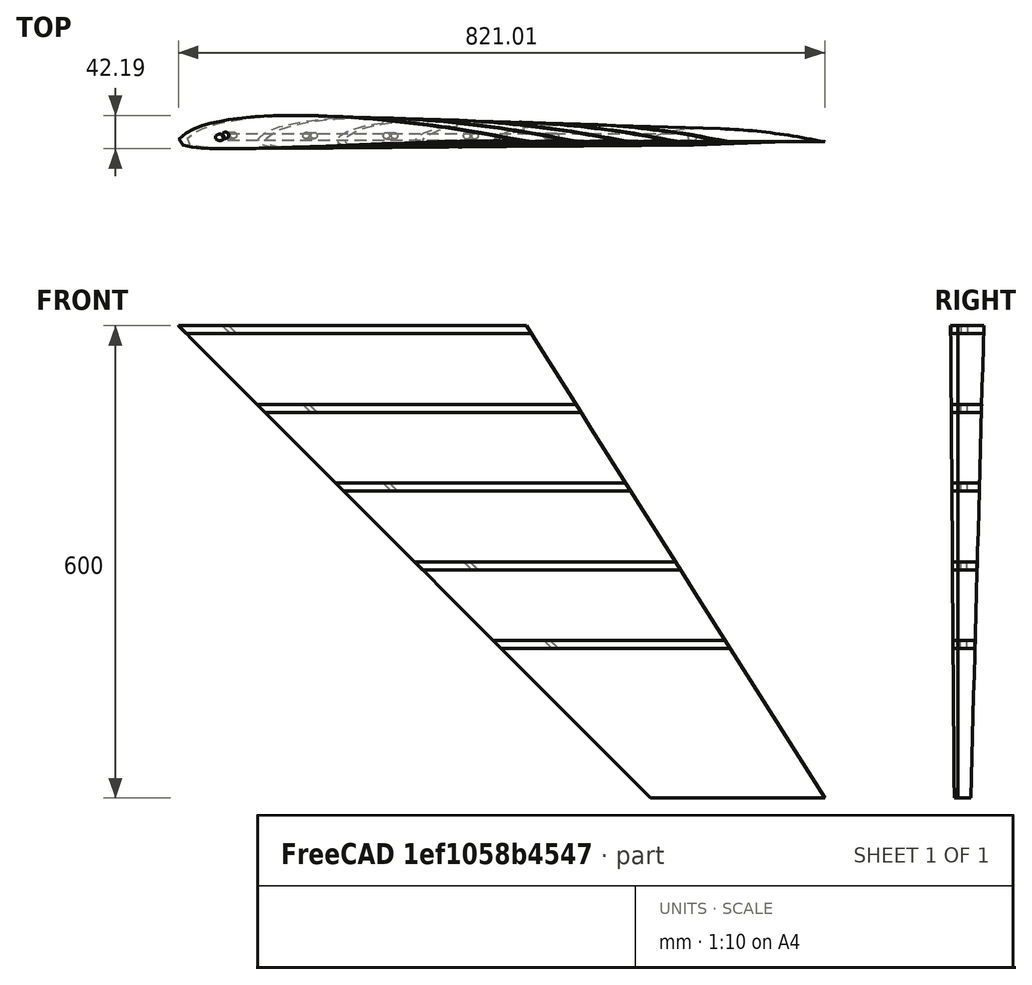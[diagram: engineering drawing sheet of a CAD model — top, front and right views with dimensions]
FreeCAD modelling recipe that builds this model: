
FCSTD DOCUMENT  (FreeCAD 1.0R39109 (Git))
Label: SD7037_the_actual_way
License: All rights reserved
LicenseURL: https://en.wikipedia.org/wiki/All_rights_reserved
objects: Sketcher::SketchObject×38, PartDesign::Pocket×12, PartDesign::AdditiveLoft×7, PartDesign::Body×7, PartDesign::SubtractiveLoft×6, Part::Part2DObjectPython×3, App::DocumentObjectGroup×1, PartDesign::Plane×1
note: 162 computed .brp shape members not serialized (recipe doc carries the construction recipe); baked Part::Feature solids carry a one-line shape summary decoded from their .brp

FEATURE [Part::Part2DObjectPython] Wire  # Draft 2D object (typed FeaturePython)
  Area = 0.0605284
  ChamferSize = 0
  Closed = true
  End = (1,0,0)
  FilletRadius = 0
  Length = 2.02979
  MakeFace = true
  Points = (61) [(1,0,0),(0.99672,0.00042,0),(0.98707,0.0018,0),(0.97146,0.00436,0),(0.95041,0.00811,0),(0.9245,0.01295,0),(0.89425,0.01865,0),(0.86015,0.0249,0),+53 more]
  Start = (1,0,0)
  Subdivisions = 0
FEATURE [App::DocumentObjectGroup] sd7037
  Group = -> [Wire]
FEATURE [Part::Part2DObjectPython] BSpline  label="wingtip"  # Draft 2D object (typed FeaturePython)
  Area = 2965.6
  Closed = true
  MakeFace = true
  Parameterization = 1
  Points = (60) [(221,0,0),(220.275,0.09282,0),(218.142,0.3978,0),(214.693,0.96356,0),(210.041,1.79231,0),(204.315,2.86195,0),(197.629,4.12165,0),(190.093,5.5029,0),+52 more]
FEATURE [Part::Part2DObjectPython] BSpline001  label="wingbase"  # Draft 2D object (typed FeaturePython)
  Area = 11862.4
  Closed = true
  MakeFace = true
  Parameterization = 1
  Points = (60) [(442,0,0),(440.55,0.18564,0),(436.285,0.7956,0),(429.385,1.92712,0),(420.081,3.58462,0),(408.629,5.7239,0),(395.258,8.2433,0),(380.186,11.0058,0),+52 more]
FEATURE [Sketcher::SketchObject] Sketch
  ArcFitTolerance = 1e-06
  FullyConstrained = false
  MakeInternals = false
  Placement = pos=(600,0,-600) rot=(0,0,1;0rad)
  sketch-geometry (123):
    g0: BSplineCurve PolesCount=61 KnotsCount=61 Degree=3 IsPeriodic=1
    g1-g61: Circle [constr] x61 (B-spline internal-alignment scaffolding for g0; pole/knot coordinates omitted)
    g62-g122: GeomPoint [constr] x61 (B-spline internal-alignment scaffolding for g0; pole/knot coordinates omitted)
  constraints (123):
    c: InternalAlignment(g1,g0)
    c: Weight(g1) = 1
    c: InternalAlignment(g2,g0)
    c: Equal(g2,g1)
    c: InternalAlignment(g3,g0)
    c: Equal(g3,g1)
    c: InternalAlignment(g4,g0)
    c: Equal(g4,g1)
    c: InternalAlignment(g5,g0)
    c: Equal(g5,g1)
    c: InternalAlignment(g6,g0)
    c: Equal(g6,g1)
    c: InternalAlignment(g7,g0)
    c: Equal(g7,g1)
    c: InternalAlignment(g8,g0)
    c: Equal(g8,g1)
    c: InternalAlignment(g9,g0)
    c: Equal(g9,g1)
    c: InternalAlignment(g10,g0)
    c: Equal(g10,g1)
    c: InternalAlignment(g11,g0)
    c: Equal(g11,g1)
    c: InternalAlignment(g12,g0)
    c: Equal(g12,g1)
    c: InternalAlignment(g13,g0)
    c: Equal(g13,g1)
    c: InternalAlignment(g14,g0)
    c: Equal(g14,g1)
    c: InternalAlignment(g15,g0)
    c: Equal(g15,g1)
    c: InternalAlignment(g16,g0)
    c: Equal(g16,g1)
    c: InternalAlignment(g17,g0)
    c: Equal(g17,g1)
    c: InternalAlignment(g18,g0)
    c: Equal(g18,g1)
    c: InternalAlignment(g19,g0)
    c: Equal(g19,g1)
    c: InternalAlignment(g20,g0)
    c: Equal(g20,g1)
    c: InternalAlignment(g21,g0)
    c: Equal(g21,g1)
    c: InternalAlignment(g22,g0)
    c: Equal(g22,g1)
    c: InternalAlignment(g23,g0)
    c: Equal(g23,g1)
    c: InternalAlignment(g24,g0)
    c: Equal(g24,g1)
    c: InternalAlignment(g25,g0)
    c: Equal(g25,g1)
    c: InternalAlignment(g26,g0)
    c: Equal(g26,g1)
    c: InternalAlignment(g27,g0)
    c: Equal(g27,g1)
    c: InternalAlignment(g28,g0)
    c: Equal(g28,g1)
    c: InternalAlignment(g29,g0)
    c: Equal(g29,g1)
    c: InternalAlignment(g30,g0)
    c: Equal(g30,g1)
    c: InternalAlignment(g31,g0)
    c: Equal(g31,g1)
    c: InternalAlignment(g32,g0)
    c: Equal(g32,g1)
    c: InternalAlignment(g33,g0)
    c: Equal(g33,g1)
    c: InternalAlignment(g34,g0)
    c: Equal(g34,g1)
    c: InternalAlignment(g35,g0)
    c: Equal(g35,g1)
    c: InternalAlignment(g36,g0)
    c: Equal(g36,g1)
    c: InternalAlignment(g37,g0)
    c: Equal(g37,g1)
    c: InternalAlignment(g38,g0)
    c: Equal(g38,g1)
    c: InternalAlignment(g39,g0)
    c: Equal(g39,g1)
    c: InternalAlignment(g40,g0)
    c: Equal(g40,g1)
    c: InternalAlignment(g41,g0)
    c: Equal(g41,g1)
    c: InternalAlignment(g42,g0)
    c: Equal(g42,g1)
    c: InternalAlignment(g43,g0)
    c: Equal(g43,g1)
    c: InternalAlignment(g44,g0)
    c: Equal(g44,g1)
    c: InternalAlignment(g45,g0)
    c: Equal(g45,g1)
    c: InternalAlignment(g46,g0)
    c: Equal(g46,g1)
    c: InternalAlignment(g47,g0)
    c: Equal(g47,g1)
    c: InternalAlignment(g48,g0)
    c: Equal(g48,g1)
    c: InternalAlignment(g49,g0)
    c: Equal(g49,g1)
    c: InternalAlignment(g50,g0)
    c: Equal(g50,g1)
    c: InternalAlignment(g51,g0)
    c: Equal(g51,g1)
    c: InternalAlignment(g52,g0)
    c: Equal(g52,g1)
    c: InternalAlignment(g53,g0)
    c: Equal(g53,g1)
    c: InternalAlignment(g54,g0)
    c: Equal(g54,g1)
    c: InternalAlignment(g55,g0)
    c: Equal(g55,g1)
    c: InternalAlignment(g56,g0)
    c: Equal(g56,g1)
    c: InternalAlignment(g57,g0)
    c: Equal(g57,g1)
    c: InternalAlignment(g58,g0)
    c: Equal(g58,g1)
    c: InternalAlignment(g59,g0)
    c: Equal(g59,g1)
    c: InternalAlignment(g60,g0)
    c: Equal(g60,g1)
    c: InternalAlignment(g61,g0)
    c: Equal(g61,g1)
    c: InternalAlignment(g62-g122 -> g0) x61
FEATURE [Sketcher::SketchObject] Sketch001
  ArcFitTolerance = 1e-06
  FullyConstrained = false
  MakeInternals = false
  sketch-geometry (123):
    g0: BSplineCurve PolesCount=61 KnotsCount=61 Degree=3 IsPeriodic=1
    g1-g61: Circle [constr] x61 (B-spline internal-alignment scaffolding for g0; pole/knot coordinates omitted)
    g62-g122: GeomPoint [constr] x61 (B-spline internal-alignment scaffolding for g0; pole/knot coordinates omitted)
  constraints (123):
    c: InternalAlignment(g1,g0)
    c: Weight(g1) = 1
    c: InternalAlignment(g2,g0)
    c: Equal(g2,g1)
    c: InternalAlignment(g3,g0)
    c: Equal(g3,g1)
    c: InternalAlignment(g4,g0)
    c: Equal(g4,g1)
    c: InternalAlignment(g5,g0)
    c: Equal(g5,g1)
    c: InternalAlignment(g6,g0)
    c: Equal(g6,g1)
    c: InternalAlignment(g7,g0)
    c: Equal(g7,g1)
    c: InternalAlignment(g8,g0)
    c: Equal(g8,g1)
    c: InternalAlignment(g9,g0)
    c: Equal(g9,g1)
    c: InternalAlignment(g10,g0)
    c: Equal(g10,g1)
    c: InternalAlignment(g11,g0)
    c: Equal(g11,g1)
    c: InternalAlignment(g12,g0)
    c: Equal(g12,g1)
    c: InternalAlignment(g13,g0)
    c: Equal(g13,g1)
    c: InternalAlignment(g14,g0)
    c: Equal(g14,g1)
    c: InternalAlignment(g15,g0)
    c: Equal(g15,g1)
    c: InternalAlignment(g16,g0)
    c: Equal(g16,g1)
    c: InternalAlignment(g17,g0)
    c: Equal(g17,g1)
    c: InternalAlignment(g18,g0)
    c: Equal(g18,g1)
    c: InternalAlignment(g19,g0)
    c: Equal(g19,g1)
    c: InternalAlignment(g20,g0)
    c: Equal(g20,g1)
    c: InternalAlignment(g21,g0)
    c: Equal(g21,g1)
    c: InternalAlignment(g22,g0)
    c: Equal(g22,g1)
    c: InternalAlignment(g23,g0)
    c: Equal(g23,g1)
    c: InternalAlignment(g24,g0)
    c: Equal(g24,g1)
    c: InternalAlignment(g25,g0)
    c: Equal(g25,g1)
    c: InternalAlignment(g26,g0)
    c: Equal(g26,g1)
    c: InternalAlignment(g27,g0)
    c: Equal(g27,g1)
    c: InternalAlignment(g28,g0)
    c: Equal(g28,g1)
    c: InternalAlignment(g29,g0)
    c: Equal(g29,g1)
    c: InternalAlignment(g30,g0)
    c: Equal(g30,g1)
    c: InternalAlignment(g31,g0)
    c: Equal(g31,g1)
    c: InternalAlignment(g32,g0)
    c: Equal(g32,g1)
    c: InternalAlignment(g33,g0)
    c: Equal(g33,g1)
    c: InternalAlignment(g34,g0)
    c: Equal(g34,g1)
    c: InternalAlignment(g35,g0)
    c: Equal(g35,g1)
    c: InternalAlignment(g36,g0)
    c: Equal(g36,g1)
    c: InternalAlignment(g37,g0)
    c: Equal(g37,g1)
    c: InternalAlignment(g38,g0)
    c: Equal(g38,g1)
    c: InternalAlignment(g39,g0)
    c: Equal(g39,g1)
    c: InternalAlignment(g40,g0)
    c: Equal(g40,g1)
    c: InternalAlignment(g41,g0)
    c: Equal(g41,g1)
    c: InternalAlignment(g42,g0)
    c: Equal(g42,g1)
    c: InternalAlignment(g43,g0)
    c: Equal(g43,g1)
    c: InternalAlignment(g44,g0)
    c: Equal(g44,g1)
    c: InternalAlignment(g45,g0)
    c: Equal(g45,g1)
    c: InternalAlignment(g46,g0)
    c: Equal(g46,g1)
    c: InternalAlignment(g47,g0)
    c: Equal(g47,g1)
    c: InternalAlignment(g48,g0)
    c: Equal(g48,g1)
    c: InternalAlignment(g49,g0)
    c: Equal(g49,g1)
    c: InternalAlignment(g50,g0)
    c: Equal(g50,g1)
    c: InternalAlignment(g51,g0)
    c: Equal(g51,g1)
    c: InternalAlignment(g52,g0)
    c: Equal(g52,g1)
    c: InternalAlignment(g53,g0)
    c: Equal(g53,g1)
    c: InternalAlignment(g54,g0)
    c: Equal(g54,g1)
    c: InternalAlignment(g55,g0)
    c: Equal(g55,g1)
    c: InternalAlignment(g56,g0)
    c: Equal(g56,g1)
    c: InternalAlignment(g57,g0)
    c: Equal(g57,g1)
    c: InternalAlignment(g58,g0)
    c: Equal(g58,g1)
    c: InternalAlignment(g59,g0)
    c: Equal(g59,g1)
    c: InternalAlignment(g60,g0)
    c: Equal(g60,g1)
    c: InternalAlignment(g61,g0)
    c: Equal(g61,g1)
    c: InternalAlignment(g62-g122 -> g0) x61
FEATURE [PartDesign::AdditiveLoft] AdditiveLoft
  Closed = false
  Profile = -> Sketch001
  Refine = true
  Ruled = false
  Sections = -> [Sketch]
  Suppressed = false
FEATURE [Sketcher::SketchObject] Sketch002
  ArcFitTolerance = 1e-06
  AttachmentSupport = -> [AdditiveLoft]
  FullyConstrained = true
  MakeInternals = false
  MapMode = 5
  sketch-geometry (1):
    g0: Circle CenterX=60 CenterY=8 CenterZ=0 NormalX=0 NormalY=0 NormalZ=1 AngleXU=0 Radius=4.025
  constraints (3):
    c: Diameter(g0) = 8.05
    c: DistanceX(g-1,g0) = 60
    c: Distance(g0,g-1) = 8
FEATURE [Sketcher::SketchObject] Sketch003
  ArcFitTolerance = 1e-06
  AttachmentSupport = -> [AdditiveLoft]
  FullyConstrained = true
  MakeInternals = false
  MapMode = 5
  Placement = pos=(0,0,-600) rot=(1,0,0;3.14159rad)
  sketch-geometry (1):
    g0: Circle CenterX=673 CenterY=-6.3 CenterZ=0 NormalX=0 NormalY=0 NormalZ=1 AngleXU=0 Radius=4.025
  constraints (3):
    c: Diameter(g0) = 8.05
    c: DistanceX(g-1,g0) = 673
    c: Distance(g0,g-1) = 6.3
FEATURE [PartDesign::SubtractiveLoft] SubtractiveLoft
  BaseFeature = -> AdditiveLoft
  Closed = false
  Profile = -> Sketch002
  Refine = true
  Ruled = false
  Sections = -> [Sketch003]
  Suppressed = false
FEATURE [Sketcher::SketchObject] Sketch004
  ArcFitTolerance = 1e-06
  FullyConstrained = false
  MakeInternals = false
  Placement = pos=(600,0,-600) rot=(0,0,1;0rad)
  sketch-geometry (123):
    g0: BSplineCurve PolesCount=61 KnotsCount=61 Degree=3 IsPeriodic=1
    g1-g61: Circle [constr] x61 (B-spline internal-alignment scaffolding for g0; pole/knot coordinates omitted)
    g62-g122: GeomPoint [constr] x61 (B-spline internal-alignment scaffolding for g0; pole/knot coordinates omitted)
  constraints (123):
    c: InternalAlignment(g1,g0)
    c: Weight(g1) = 1
    c: InternalAlignment(g2,g0)
    c: Equal(g2,g1)
    c: InternalAlignment(g3,g0)
    c: Equal(g3,g1)
    c: InternalAlignment(g4,g0)
    c: Equal(g4,g1)
    c: InternalAlignment(g5,g0)
    c: Equal(g5,g1)
    c: InternalAlignment(g6,g0)
    c: Equal(g6,g1)
    c: InternalAlignment(g7,g0)
    c: Equal(g7,g1)
    c: InternalAlignment(g8,g0)
    c: Equal(g8,g1)
    c: InternalAlignment(g9,g0)
    c: Equal(g9,g1)
    c: InternalAlignment(g10,g0)
    c: Equal(g10,g1)
    c: InternalAlignment(g11,g0)
    c: Equal(g11,g1)
    c: InternalAlignment(g12,g0)
    c: Equal(g12,g1)
    c: InternalAlignment(g13,g0)
    c: Equal(g13,g1)
    c: InternalAlignment(g14,g0)
    c: Equal(g14,g1)
    c: InternalAlignment(g15,g0)
    c: Equal(g15,g1)
    c: InternalAlignment(g16,g0)
    c: Equal(g16,g1)
    c: InternalAlignment(g17,g0)
    c: Equal(g17,g1)
    c: InternalAlignment(g18,g0)
    c: Equal(g18,g1)
    c: InternalAlignment(g19,g0)
    c: Equal(g19,g1)
    c: InternalAlignment(g20,g0)
    c: Equal(g20,g1)
    c: InternalAlignment(g21,g0)
    c: Equal(g21,g1)
    c: InternalAlignment(g22,g0)
    c: Equal(g22,g1)
    c: InternalAlignment(g23,g0)
    c: Equal(g23,g1)
    c: InternalAlignment(g24,g0)
    c: Equal(g24,g1)
    c: InternalAlignment(g25,g0)
    c: Equal(g25,g1)
    c: InternalAlignment(g26,g0)
    c: Equal(g26,g1)
    c: InternalAlignment(g27,g0)
    c: Equal(g27,g1)
    c: InternalAlignment(g28,g0)
    c: Equal(g28,g1)
    c: InternalAlignment(g29,g0)
    c: Equal(g29,g1)
    c: InternalAlignment(g30,g0)
    c: Equal(g30,g1)
    c: InternalAlignment(g31,g0)
    c: Equal(g31,g1)
    c: InternalAlignment(g32,g0)
    c: Equal(g32,g1)
    c: InternalAlignment(g33,g0)
    c: Equal(g33,g1)
    c: InternalAlignment(g34,g0)
    c: Equal(g34,g1)
    c: InternalAlignment(g35,g0)
    c: Equal(g35,g1)
    c: InternalAlignment(g36,g0)
    c: Equal(g36,g1)
    c: InternalAlignment(g37,g0)
    c: Equal(g37,g1)
    c: InternalAlignment(g38,g0)
    c: Equal(g38,g1)
    c: InternalAlignment(g39,g0)
    c: Equal(g39,g1)
    c: InternalAlignment(g40,g0)
    c: Equal(g40,g1)
    c: InternalAlignment(g41,g0)
    c: Equal(g41,g1)
    c: InternalAlignment(g42,g0)
    c: Equal(g42,g1)
    c: InternalAlignment(g43,g0)
    c: Equal(g43,g1)
    c: InternalAlignment(g44,g0)
    c: Equal(g44,g1)
    c: InternalAlignment(g45,g0)
    c: Equal(g45,g1)
    c: InternalAlignment(g46,g0)
    c: Equal(g46,g1)
    c: InternalAlignment(g47,g0)
    c: Equal(g47,g1)
    c: InternalAlignment(g48,g0)
    c: Equal(g48,g1)
    c: InternalAlignment(g49,g0)
    c: Equal(g49,g1)
    c: InternalAlignment(g50,g0)
    c: Equal(g50,g1)
    c: InternalAlignment(g51,g0)
    c: Equal(g51,g1)
    c: InternalAlignment(g52,g0)
    c: Equal(g52,g1)
    c: InternalAlignment(g53,g0)
    c: Equal(g53,g1)
    c: InternalAlignment(g54,g0)
    c: Equal(g54,g1)
    c: InternalAlignment(g55,g0)
    c: Equal(g55,g1)
    c: InternalAlignment(g56,g0)
    c: Equal(g56,g1)
    c: InternalAlignment(g57,g0)
    c: Equal(g57,g1)
    c: InternalAlignment(g58,g0)
    c: Equal(g58,g1)
    c: InternalAlignment(g59,g0)
    c: Equal(g59,g1)
    c: InternalAlignment(g60,g0)
    c: Equal(g60,g1)
    c: InternalAlignment(g61,g0)
    c: Equal(g61,g1)
    c: InternalAlignment(g62-g122 -> g0) x61
FEATURE [Sketcher::SketchObject] Sketch005
  ArcFitTolerance = 1e-06
  FullyConstrained = false
  MakeInternals = false
  sketch-geometry (123):
    g0: BSplineCurve PolesCount=61 KnotsCount=61 Degree=3 IsPeriodic=1
    g1-g61: Circle [constr] x61 (B-spline internal-alignment scaffolding for g0; pole/knot coordinates omitted)
    g62-g122: GeomPoint [constr] x61 (B-spline internal-alignment scaffolding for g0; pole/knot coordinates omitted)
  constraints (123):
    c: InternalAlignment(g1,g0)
    c: Weight(g1) = 1
    c: InternalAlignment(g2,g0)
    c: Equal(g2,g1)
    c: InternalAlignment(g3,g0)
    c: Equal(g3,g1)
    c: InternalAlignment(g4,g0)
    c: Equal(g4,g1)
    c: InternalAlignment(g5,g0)
    c: Equal(g5,g1)
    c: InternalAlignment(g6,g0)
    c: Equal(g6,g1)
    c: InternalAlignment(g7,g0)
    c: Equal(g7,g1)
    c: InternalAlignment(g8,g0)
    c: Equal(g8,g1)
    c: InternalAlignment(g9,g0)
    c: Equal(g9,g1)
    c: InternalAlignment(g10,g0)
    c: Equal(g10,g1)
    c: InternalAlignment(g11,g0)
    c: Equal(g11,g1)
    c: InternalAlignment(g12,g0)
    c: Equal(g12,g1)
    c: InternalAlignment(g13,g0)
    c: Equal(g13,g1)
    c: InternalAlignment(g14,g0)
    c: Equal(g14,g1)
    c: InternalAlignment(g15,g0)
    c: Equal(g15,g1)
    c: InternalAlignment(g16,g0)
    c: Equal(g16,g1)
    c: InternalAlignment(g17,g0)
    c: Equal(g17,g1)
    c: InternalAlignment(g18,g0)
    c: Equal(g18,g1)
    c: InternalAlignment(g19,g0)
    c: Equal(g19,g1)
    c: InternalAlignment(g20,g0)
    c: Equal(g20,g1)
    c: InternalAlignment(g21,g0)
    c: Equal(g21,g1)
    c: InternalAlignment(g22,g0)
    c: Equal(g22,g1)
    c: InternalAlignment(g23,g0)
    c: Equal(g23,g1)
    c: InternalAlignment(g24,g0)
    c: Equal(g24,g1)
    c: InternalAlignment(g25,g0)
    c: Equal(g25,g1)
    c: InternalAlignment(g26,g0)
    c: Equal(g26,g1)
    c: InternalAlignment(g27,g0)
    c: Equal(g27,g1)
    c: InternalAlignment(g28,g0)
    c: Equal(g28,g1)
    c: InternalAlignment(g29,g0)
    c: Equal(g29,g1)
    c: InternalAlignment(g30,g0)
    c: Equal(g30,g1)
    c: InternalAlignment(g31,g0)
    c: Equal(g31,g1)
    c: InternalAlignment(g32,g0)
    c: Equal(g32,g1)
    c: InternalAlignment(g33,g0)
    c: Equal(g33,g1)
    c: InternalAlignment(g34,g0)
    c: Equal(g34,g1)
    c: InternalAlignment(g35,g0)
    c: Equal(g35,g1)
    c: InternalAlignment(g36,g0)
    c: Equal(g36,g1)
    c: InternalAlignment(g37,g0)
    c: Equal(g37,g1)
    c: InternalAlignment(g38,g0)
    c: Equal(g38,g1)
    c: InternalAlignment(g39,g0)
    c: Equal(g39,g1)
    c: InternalAlignment(g40,g0)
    c: Equal(g40,g1)
    c: InternalAlignment(g41,g0)
    c: Equal(g41,g1)
    c: InternalAlignment(g42,g0)
    c: Equal(g42,g1)
    c: InternalAlignment(g43,g0)
    c: Equal(g43,g1)
    c: InternalAlignment(g44,g0)
    c: Equal(g44,g1)
    c: InternalAlignment(g45,g0)
    c: Equal(g45,g1)
    c: InternalAlignment(g46,g0)
    c: Equal(g46,g1)
    c: InternalAlignment(g47,g0)
    c: Equal(g47,g1)
    c: InternalAlignment(g48,g0)
    c: Equal(g48,g1)
    c: InternalAlignment(g49,g0)
    c: Equal(g49,g1)
    c: InternalAlignment(g50,g0)
    c: Equal(g50,g1)
    c: InternalAlignment(g51,g0)
    c: Equal(g51,g1)
    c: InternalAlignment(g52,g0)
    c: Equal(g52,g1)
    c: InternalAlignment(g53,g0)
    c: Equal(g53,g1)
    c: InternalAlignment(g54,g0)
    c: Equal(g54,g1)
    c: InternalAlignment(g55,g0)
    c: Equal(g55,g1)
    c: InternalAlignment(g56,g0)
    c: Equal(g56,g1)
    c: InternalAlignment(g57,g0)
    c: Equal(g57,g1)
    c: InternalAlignment(g58,g0)
    c: Equal(g58,g1)
    c: InternalAlignment(g59,g0)
    c: Equal(g59,g1)
    c: InternalAlignment(g60,g0)
    c: Equal(g60,g1)
    c: InternalAlignment(g61,g0)
    c: Equal(g61,g1)
    c: InternalAlignment(g62-g122 -> g0) x61
FEATURE [PartDesign::AdditiveLoft] AdditiveLoft001
  Closed = false
  Profile = -> Sketch005
  Refine = true
  Ruled = false
  Sections = -> [Sketch004]
  Suppressed = false
FEATURE [Sketcher::SketchObject] Sketch006
  ArcFitTolerance = 1e-06
  AttachmentSupport = -> [AdditiveLoft001]
  FullyConstrained = true
  MakeInternals = false
  MapMode = 5
  sketch-geometry (1):
    g0: Circle CenterX=60 CenterY=8 CenterZ=0 NormalX=0 NormalY=0 NormalZ=1 AngleXU=0 Radius=4.025
  constraints (3):
    c: Diameter(g0) = 8.05
    c: DistanceX(g-1,g0) = 60
    c: Distance(g0,g-1) = 8
FEATURE [Sketcher::SketchObject] Sketch007
  ArcFitTolerance = 1e-06
  AttachmentSupport = -> [AdditiveLoft001]
  FullyConstrained = true
  MakeInternals = false
  MapMode = 5
  Placement = pos=(0,0,-600) rot=(1,0,0;3.14159rad)
  sketch-geometry (1):
    g0: Circle CenterX=673 CenterY=-6.3 CenterZ=0 NormalX=0 NormalY=0 NormalZ=1 AngleXU=0 Radius=4.025
  constraints (3):
    c: Diameter(g0) = 8.05
    c: DistanceX(g-1,g0) = 673
    c: Distance(g0,g-1) = 6.3
FEATURE [PartDesign::SubtractiveLoft] SubtractiveLoft001
  BaseFeature = -> AdditiveLoft001
  Closed = false
  Profile = -> Sketch006
  Refine = true
  Ruled = false
  Sections = -> [Sketch007]
  Suppressed = false
FEATURE [Sketcher::SketchObject] Sketch008
  ArcFitTolerance = 1e-06
  FullyConstrained = false
  MakeInternals = false
  Placement = pos=(600,0,-600) rot=(0,0,1;0rad)
  sketch-geometry (123):
    g0: BSplineCurve PolesCount=61 KnotsCount=61 Degree=3 IsPeriodic=1
    g1-g61: Circle [constr] x61 (B-spline internal-alignment scaffolding for g0; pole/knot coordinates omitted)
    g62-g122: GeomPoint [constr] x61 (B-spline internal-alignment scaffolding for g0; pole/knot coordinates omitted)
  constraints (123):
    c: InternalAlignment(g1,g0)
    c: Weight(g1) = 1
    c: InternalAlignment(g2,g0)
    c: Equal(g2,g1)
    c: InternalAlignment(g3,g0)
    c: Equal(g3,g1)
    c: InternalAlignment(g4,g0)
    c: Equal(g4,g1)
    c: InternalAlignment(g5,g0)
    c: Equal(g5,g1)
    c: InternalAlignment(g6,g0)
    c: Equal(g6,g1)
    c: InternalAlignment(g7,g0)
    c: Equal(g7,g1)
    c: InternalAlignment(g8,g0)
    c: Equal(g8,g1)
    c: InternalAlignment(g9,g0)
    c: Equal(g9,g1)
    c: InternalAlignment(g10,g0)
    c: Equal(g10,g1)
    c: InternalAlignment(g11,g0)
    c: Equal(g11,g1)
    c: InternalAlignment(g12,g0)
    c: Equal(g12,g1)
    c: InternalAlignment(g13,g0)
    c: Equal(g13,g1)
    c: InternalAlignment(g14,g0)
    c: Equal(g14,g1)
    c: InternalAlignment(g15,g0)
    c: Equal(g15,g1)
    c: InternalAlignment(g16,g0)
    c: Equal(g16,g1)
    c: InternalAlignment(g17,g0)
    c: Equal(g17,g1)
    c: InternalAlignment(g18,g0)
    c: Equal(g18,g1)
    c: InternalAlignment(g19,g0)
    c: Equal(g19,g1)
    c: InternalAlignment(g20,g0)
    c: Equal(g20,g1)
    c: InternalAlignment(g21,g0)
    c: Equal(g21,g1)
    c: InternalAlignment(g22,g0)
    c: Equal(g22,g1)
    c: InternalAlignment(g23,g0)
    c: Equal(g23,g1)
    c: InternalAlignment(g24,g0)
    c: Equal(g24,g1)
    c: InternalAlignment(g25,g0)
    c: Equal(g25,g1)
    c: InternalAlignment(g26,g0)
    c: Equal(g26,g1)
    c: InternalAlignment(g27,g0)
    c: Equal(g27,g1)
    c: InternalAlignment(g28,g0)
    c: Equal(g28,g1)
    c: InternalAlignment(g29,g0)
    c: Equal(g29,g1)
    c: InternalAlignment(g30,g0)
    c: Equal(g30,g1)
    c: InternalAlignment(g31,g0)
    c: Equal(g31,g1)
    c: InternalAlignment(g32,g0)
    c: Equal(g32,g1)
    c: InternalAlignment(g33,g0)
    c: Equal(g33,g1)
    c: InternalAlignment(g34,g0)
    c: Equal(g34,g1)
    c: InternalAlignment(g35,g0)
    c: Equal(g35,g1)
    c: InternalAlignment(g36,g0)
    c: Equal(g36,g1)
    c: InternalAlignment(g37,g0)
    c: Equal(g37,g1)
    c: InternalAlignment(g38,g0)
    c: Equal(g38,g1)
    c: InternalAlignment(g39,g0)
    c: Equal(g39,g1)
    c: InternalAlignment(g40,g0)
    c: Equal(g40,g1)
    c: InternalAlignment(g41,g0)
    c: Equal(g41,g1)
    c: InternalAlignment(g42,g0)
    c: Equal(g42,g1)
    c: InternalAlignment(g43,g0)
    c: Equal(g43,g1)
    c: InternalAlignment(g44,g0)
    c: Equal(g44,g1)
    c: InternalAlignment(g45,g0)
    c: Equal(g45,g1)
    c: InternalAlignment(g46,g0)
    c: Equal(g46,g1)
    c: InternalAlignment(g47,g0)
    c: Equal(g47,g1)
    c: InternalAlignment(g48,g0)
    c: Equal(g48,g1)
    c: InternalAlignment(g49,g0)
    c: Equal(g49,g1)
    c: InternalAlignment(g50,g0)
    c: Equal(g50,g1)
    c: InternalAlignment(g51,g0)
    c: Equal(g51,g1)
    c: InternalAlignment(g52,g0)
    c: Equal(g52,g1)
    c: InternalAlignment(g53,g0)
    c: Equal(g53,g1)
    c: InternalAlignment(g54,g0)
    c: Equal(g54,g1)
    c: InternalAlignment(g55,g0)
    c: Equal(g55,g1)
    c: InternalAlignment(g56,g0)
    c: Equal(g56,g1)
    c: InternalAlignment(g57,g0)
    c: Equal(g57,g1)
    c: InternalAlignment(g58,g0)
    c: Equal(g58,g1)
    c: InternalAlignment(g59,g0)
    c: Equal(g59,g1)
    c: InternalAlignment(g60,g0)
    c: Equal(g60,g1)
    c: InternalAlignment(g61,g0)
    c: Equal(g61,g1)
    c: InternalAlignment(g62-g122 -> g0) x61
FEATURE [Sketcher::SketchObject] Sketch009
  ArcFitTolerance = 1e-06
  FullyConstrained = false
  MakeInternals = false
  sketch-geometry (123):
    g0: BSplineCurve PolesCount=61 KnotsCount=61 Degree=3 IsPeriodic=1
    g1-g61: Circle [constr] x61 (B-spline internal-alignment scaffolding for g0; pole/knot coordinates omitted)
    g62-g122: GeomPoint [constr] x61 (B-spline internal-alignment scaffolding for g0; pole/knot coordinates omitted)
  constraints (123):
    c: InternalAlignment(g1,g0)
    c: Weight(g1) = 1
    c: InternalAlignment(g2,g0)
    c: Equal(g2,g1)
    c: InternalAlignment(g3,g0)
    c: Equal(g3,g1)
    c: InternalAlignment(g4,g0)
    c: Equal(g4,g1)
    c: InternalAlignment(g5,g0)
    c: Equal(g5,g1)
    c: InternalAlignment(g6,g0)
    c: Equal(g6,g1)
    c: InternalAlignment(g7,g0)
    c: Equal(g7,g1)
    c: InternalAlignment(g8,g0)
    c: Equal(g8,g1)
    c: InternalAlignment(g9,g0)
    c: Equal(g9,g1)
    c: InternalAlignment(g10,g0)
    c: Equal(g10,g1)
    c: InternalAlignment(g11,g0)
    c: Equal(g11,g1)
    c: InternalAlignment(g12,g0)
    c: Equal(g12,g1)
    c: InternalAlignment(g13,g0)
    c: Equal(g13,g1)
    c: InternalAlignment(g14,g0)
    c: Equal(g14,g1)
    c: InternalAlignment(g15,g0)
    c: Equal(g15,g1)
    c: InternalAlignment(g16,g0)
    c: Equal(g16,g1)
    c: InternalAlignment(g17,g0)
    c: Equal(g17,g1)
    c: InternalAlignment(g18,g0)
    c: Equal(g18,g1)
    c: InternalAlignment(g19,g0)
    c: Equal(g19,g1)
    c: InternalAlignment(g20,g0)
    c: Equal(g20,g1)
    c: InternalAlignment(g21,g0)
    c: Equal(g21,g1)
    c: InternalAlignment(g22,g0)
    c: Equal(g22,g1)
    c: InternalAlignment(g23,g0)
    c: Equal(g23,g1)
    c: InternalAlignment(g24,g0)
    c: Equal(g24,g1)
    c: InternalAlignment(g25,g0)
    c: Equal(g25,g1)
    c: InternalAlignment(g26,g0)
    c: Equal(g26,g1)
    c: InternalAlignment(g27,g0)
    c: Equal(g27,g1)
    c: InternalAlignment(g28,g0)
    c: Equal(g28,g1)
    c: InternalAlignment(g29,g0)
    c: Equal(g29,g1)
    c: InternalAlignment(g30,g0)
    c: Equal(g30,g1)
    c: InternalAlignment(g31,g0)
    c: Equal(g31,g1)
    c: InternalAlignment(g32,g0)
    c: Equal(g32,g1)
    c: InternalAlignment(g33,g0)
    c: Equal(g33,g1)
    c: InternalAlignment(g34,g0)
    c: Equal(g34,g1)
    c: InternalAlignment(g35,g0)
    c: Equal(g35,g1)
    c: InternalAlignment(g36,g0)
    c: Equal(g36,g1)
    c: InternalAlignment(g37,g0)
    c: Equal(g37,g1)
    c: InternalAlignment(g38,g0)
    c: Equal(g38,g1)
    c: InternalAlignment(g39,g0)
    c: Equal(g39,g1)
    c: InternalAlignment(g40,g0)
    c: Equal(g40,g1)
    c: InternalAlignment(g41,g0)
    c: Equal(g41,g1)
    c: InternalAlignment(g42,g0)
    c: Equal(g42,g1)
    c: InternalAlignment(g43,g0)
    c: Equal(g43,g1)
    c: InternalAlignment(g44,g0)
    c: Equal(g44,g1)
    c: InternalAlignment(g45,g0)
    c: Equal(g45,g1)
    c: InternalAlignment(g46,g0)
    c: Equal(g46,g1)
    c: InternalAlignment(g47,g0)
    c: Equal(g47,g1)
    c: InternalAlignment(g48,g0)
    c: Equal(g48,g1)
    c: InternalAlignment(g49,g0)
    c: Equal(g49,g1)
    c: InternalAlignment(g50,g0)
    c: Equal(g50,g1)
    c: InternalAlignment(g51,g0)
    c: Equal(g51,g1)
    c: InternalAlignment(g52,g0)
    c: Equal(g52,g1)
    c: InternalAlignment(g53,g0)
    c: Equal(g53,g1)
    c: InternalAlignment(g54,g0)
    c: Equal(g54,g1)
    c: InternalAlignment(g55,g0)
    c: Equal(g55,g1)
    c: InternalAlignment(g56,g0)
    c: Equal(g56,g1)
    c: InternalAlignment(g57,g0)
    c: Equal(g57,g1)
    c: InternalAlignment(g58,g0)
    c: Equal(g58,g1)
    c: InternalAlignment(g59,g0)
    c: Equal(g59,g1)
    c: InternalAlignment(g60,g0)
    c: Equal(g60,g1)
    c: InternalAlignment(g61,g0)
    c: Equal(g61,g1)
    c: InternalAlignment(g62-g122 -> g0) x61
FEATURE [PartDesign::AdditiveLoft] AdditiveLoft002
  Closed = false
  Profile = -> Sketch009
  Refine = true
  Ruled = false
  Sections = -> [Sketch008]
  Suppressed = false
FEATURE [Sketcher::SketchObject] Sketch010
  ArcFitTolerance = 1e-06
  AttachmentSupport = -> [AdditiveLoft002]
  FullyConstrained = true
  MakeInternals = false
  MapMode = 5
  sketch-geometry (1):
    g0: Circle CenterX=60 CenterY=8 CenterZ=0 NormalX=0 NormalY=0 NormalZ=1 AngleXU=0 Radius=4.025
  constraints (3):
    c: Diameter(g0) = 8.05
    c: DistanceX(g-1,g0) = 60
    c: Distance(g0,g-1) = 8
FEATURE [Sketcher::SketchObject] Sketch011
  ArcFitTolerance = 1e-06
  AttachmentSupport = -> [AdditiveLoft002]
  FullyConstrained = true
  MakeInternals = false
  MapMode = 5
  Placement = pos=(0,0,-600) rot=(1,0,0;3.14159rad)
  sketch-geometry (1):
    g0: Circle CenterX=673 CenterY=-6.3 CenterZ=0 NormalX=0 NormalY=0 NormalZ=1 AngleXU=0 Radius=4.025
  constraints (3):
    c: Diameter(g0) = 8.05
    c: DistanceX(g-1,g0) = 673
    c: Distance(g0,g-1) = 6.3
FEATURE [PartDesign::SubtractiveLoft] SubtractiveLoft002
  BaseFeature = -> AdditiveLoft002
  Closed = false
  Profile = -> Sketch010
  Refine = true
  Ruled = false
  Sections = -> [Sketch011]
  Suppressed = false
FEATURE [Sketcher::SketchObject] Sketch012
  ArcFitTolerance = 1e-06
  FullyConstrained = false
  MakeInternals = false
  Placement = pos=(600,0,-600) rot=(0,0,1;0rad)
  sketch-geometry (123):
    g0: BSplineCurve PolesCount=61 KnotsCount=61 Degree=3 IsPeriodic=1
    g1-g61: Circle [constr] x61 (B-spline internal-alignment scaffolding for g0; pole/knot coordinates omitted)
    g62-g122: GeomPoint [constr] x61 (B-spline internal-alignment scaffolding for g0; pole/knot coordinates omitted)
  constraints (123):
    c: InternalAlignment(g1,g0)
    c: Weight(g1) = 1
    c: InternalAlignment(g2,g0)
    c: Equal(g2,g1)
    c: InternalAlignment(g3,g0)
    c: Equal(g3,g1)
    c: InternalAlignment(g4,g0)
    c: Equal(g4,g1)
    c: InternalAlignment(g5,g0)
    c: Equal(g5,g1)
    c: InternalAlignment(g6,g0)
    c: Equal(g6,g1)
    c: InternalAlignment(g7,g0)
    c: Equal(g7,g1)
    c: InternalAlignment(g8,g0)
    c: Equal(g8,g1)
    c: InternalAlignment(g9,g0)
    c: Equal(g9,g1)
    c: InternalAlignment(g10,g0)
    c: Equal(g10,g1)
    c: InternalAlignment(g11,g0)
    c: Equal(g11,g1)
    c: InternalAlignment(g12,g0)
    c: Equal(g12,g1)
    c: InternalAlignment(g13,g0)
    c: Equal(g13,g1)
    c: InternalAlignment(g14,g0)
    c: Equal(g14,g1)
    c: InternalAlignment(g15,g0)
    c: Equal(g15,g1)
    c: InternalAlignment(g16,g0)
    c: Equal(g16,g1)
    c: InternalAlignment(g17,g0)
    c: Equal(g17,g1)
    c: InternalAlignment(g18,g0)
    c: Equal(g18,g1)
    c: InternalAlignment(g19,g0)
    c: Equal(g19,g1)
    c: InternalAlignment(g20,g0)
    c: Equal(g20,g1)
    c: InternalAlignment(g21,g0)
    c: Equal(g21,g1)
    c: InternalAlignment(g22,g0)
    c: Equal(g22,g1)
    c: InternalAlignment(g23,g0)
    c: Equal(g23,g1)
    c: InternalAlignment(g24,g0)
    c: Equal(g24,g1)
    c: InternalAlignment(g25,g0)
    c: Equal(g25,g1)
    c: InternalAlignment(g26,g0)
    c: Equal(g26,g1)
    c: InternalAlignment(g27,g0)
    c: Equal(g27,g1)
    c: InternalAlignment(g28,g0)
    c: Equal(g28,g1)
    c: InternalAlignment(g29,g0)
    c: Equal(g29,g1)
    c: InternalAlignment(g30,g0)
    c: Equal(g30,g1)
    c: InternalAlignment(g31,g0)
    c: Equal(g31,g1)
    c: InternalAlignment(g32,g0)
    c: Equal(g32,g1)
    c: InternalAlignment(g33,g0)
    c: Equal(g33,g1)
    c: InternalAlignment(g34,g0)
    c: Equal(g34,g1)
    c: InternalAlignment(g35,g0)
    c: Equal(g35,g1)
    c: InternalAlignment(g36,g0)
    c: Equal(g36,g1)
    c: InternalAlignment(g37,g0)
    c: Equal(g37,g1)
    c: InternalAlignment(g38,g0)
    c: Equal(g38,g1)
    c: InternalAlignment(g39,g0)
    c: Equal(g39,g1)
    c: InternalAlignment(g40,g0)
    c: Equal(g40,g1)
    c: InternalAlignment(g41,g0)
    c: Equal(g41,g1)
    c: InternalAlignment(g42,g0)
    c: Equal(g42,g1)
    c: InternalAlignment(g43,g0)
    c: Equal(g43,g1)
    c: InternalAlignment(g44,g0)
    c: Equal(g44,g1)
    c: InternalAlignment(g45,g0)
    c: Equal(g45,g1)
    c: InternalAlignment(g46,g0)
    c: Equal(g46,g1)
    c: InternalAlignment(g47,g0)
    c: Equal(g47,g1)
    c: InternalAlignment(g48,g0)
    c: Equal(g48,g1)
    c: InternalAlignment(g49,g0)
    c: Equal(g49,g1)
    c: InternalAlignment(g50,g0)
    c: Equal(g50,g1)
    c: InternalAlignment(g51,g0)
    c: Equal(g51,g1)
    c: InternalAlignment(g52,g0)
    c: Equal(g52,g1)
    c: InternalAlignment(g53,g0)
    c: Equal(g53,g1)
    c: InternalAlignment(g54,g0)
    c: Equal(g54,g1)
    c: InternalAlignment(g55,g0)
    c: Equal(g55,g1)
    c: InternalAlignment(g56,g0)
    c: Equal(g56,g1)
    c: InternalAlignment(g57,g0)
    c: Equal(g57,g1)
    c: InternalAlignment(g58,g0)
    c: Equal(g58,g1)
    c: InternalAlignment(g59,g0)
    c: Equal(g59,g1)
    c: InternalAlignment(g60,g0)
    c: Equal(g60,g1)
    c: InternalAlignment(g61,g0)
    c: Equal(g61,g1)
    c: InternalAlignment(g62-g122 -> g0) x61
FEATURE [Sketcher::SketchObject] Sketch013
  ArcFitTolerance = 1e-06
  FullyConstrained = false
  MakeInternals = false
  sketch-geometry (123):
    g0: BSplineCurve PolesCount=61 KnotsCount=61 Degree=3 IsPeriodic=1
    g1-g61: Circle [constr] x61 (B-spline internal-alignment scaffolding for g0; pole/knot coordinates omitted)
    g62-g122: GeomPoint [constr] x61 (B-spline internal-alignment scaffolding for g0; pole/knot coordinates omitted)
  constraints (123):
    c: InternalAlignment(g1,g0)
    c: Weight(g1) = 1
    c: InternalAlignment(g2,g0)
    c: Equal(g2,g1)
    c: InternalAlignment(g3,g0)
    c: Equal(g3,g1)
    c: InternalAlignment(g4,g0)
    c: Equal(g4,g1)
    c: InternalAlignment(g5,g0)
    c: Equal(g5,g1)
    c: InternalAlignment(g6,g0)
    c: Equal(g6,g1)
    c: InternalAlignment(g7,g0)
    c: Equal(g7,g1)
    c: InternalAlignment(g8,g0)
    c: Equal(g8,g1)
    c: InternalAlignment(g9,g0)
    c: Equal(g9,g1)
    c: InternalAlignment(g10,g0)
    c: Equal(g10,g1)
    c: InternalAlignment(g11,g0)
    c: Equal(g11,g1)
    c: InternalAlignment(g12,g0)
    c: Equal(g12,g1)
    c: InternalAlignment(g13,g0)
    c: Equal(g13,g1)
    c: InternalAlignment(g14,g0)
    c: Equal(g14,g1)
    c: InternalAlignment(g15,g0)
    c: Equal(g15,g1)
    c: InternalAlignment(g16,g0)
    c: Equal(g16,g1)
    c: InternalAlignment(g17,g0)
    c: Equal(g17,g1)
    c: InternalAlignment(g18,g0)
    c: Equal(g18,g1)
    c: InternalAlignment(g19,g0)
    c: Equal(g19,g1)
    c: InternalAlignment(g20,g0)
    c: Equal(g20,g1)
    c: InternalAlignment(g21,g0)
    c: Equal(g21,g1)
    c: InternalAlignment(g22,g0)
    c: Equal(g22,g1)
    c: InternalAlignment(g23,g0)
    c: Equal(g23,g1)
    c: InternalAlignment(g24,g0)
    c: Equal(g24,g1)
    c: InternalAlignment(g25,g0)
    c: Equal(g25,g1)
    c: InternalAlignment(g26,g0)
    c: Equal(g26,g1)
    c: InternalAlignment(g27,g0)
    c: Equal(g27,g1)
    c: InternalAlignment(g28,g0)
    c: Equal(g28,g1)
    c: InternalAlignment(g29,g0)
    c: Equal(g29,g1)
    c: InternalAlignment(g30,g0)
    c: Equal(g30,g1)
    c: InternalAlignment(g31,g0)
    c: Equal(g31,g1)
    c: InternalAlignment(g32,g0)
    c: Equal(g32,g1)
    c: InternalAlignment(g33,g0)
    c: Equal(g33,g1)
    c: InternalAlignment(g34,g0)
    c: Equal(g34,g1)
    c: InternalAlignment(g35,g0)
    c: Equal(g35,g1)
    c: InternalAlignment(g36,g0)
    c: Equal(g36,g1)
    c: InternalAlignment(g37,g0)
    c: Equal(g37,g1)
    c: InternalAlignment(g38,g0)
    c: Equal(g38,g1)
    c: InternalAlignment(g39,g0)
    c: Equal(g39,g1)
    c: InternalAlignment(g40,g0)
    c: Equal(g40,g1)
    c: InternalAlignment(g41,g0)
    c: Equal(g41,g1)
    c: InternalAlignment(g42,g0)
    c: Equal(g42,g1)
    c: InternalAlignment(g43,g0)
    c: Equal(g43,g1)
    c: InternalAlignment(g44,g0)
    c: Equal(g44,g1)
    c: InternalAlignment(g45,g0)
    c: Equal(g45,g1)
    c: InternalAlignment(g46,g0)
    c: Equal(g46,g1)
    c: InternalAlignment(g47,g0)
    c: Equal(g47,g1)
    c: InternalAlignment(g48,g0)
    c: Equal(g48,g1)
    c: InternalAlignment(g49,g0)
    c: Equal(g49,g1)
    c: InternalAlignment(g50,g0)
    c: Equal(g50,g1)
    c: InternalAlignment(g51,g0)
    c: Equal(g51,g1)
    c: InternalAlignment(g52,g0)
    c: Equal(g52,g1)
    c: InternalAlignment(g53,g0)
    c: Equal(g53,g1)
    c: InternalAlignment(g54,g0)
    c: Equal(g54,g1)
    c: InternalAlignment(g55,g0)
    c: Equal(g55,g1)
    c: InternalAlignment(g56,g0)
    c: Equal(g56,g1)
    c: InternalAlignment(g57,g0)
    c: Equal(g57,g1)
    c: InternalAlignment(g58,g0)
    c: Equal(g58,g1)
    c: InternalAlignment(g59,g0)
    c: Equal(g59,g1)
    c: InternalAlignment(g60,g0)
    c: Equal(g60,g1)
    c: InternalAlignment(g61,g0)
    c: Equal(g61,g1)
    c: InternalAlignment(g62-g122 -> g0) x61
FEATURE [PartDesign::AdditiveLoft] AdditiveLoft003
  Closed = false
  Profile = -> Sketch013
  Refine = true
  Ruled = false
  Sections = -> [Sketch012]
  Suppressed = false
FEATURE [Sketcher::SketchObject] Sketch014
  ArcFitTolerance = 1e-06
  AttachmentSupport = -> [AdditiveLoft003]
  FullyConstrained = true
  MakeInternals = false
  MapMode = 5
  sketch-geometry (1):
    g0: Circle CenterX=60 CenterY=8 CenterZ=0 NormalX=0 NormalY=0 NormalZ=1 AngleXU=0 Radius=4.025
  constraints (3):
    c: Diameter(g0) = 8.05
    c: DistanceX(g-1,g0) = 60
    c: Distance(g0,g-1) = 8
FEATURE [Sketcher::SketchObject] Sketch015
  ArcFitTolerance = 1e-06
  AttachmentSupport = -> [AdditiveLoft003]
  FullyConstrained = true
  MakeInternals = false
  MapMode = 5
  Placement = pos=(0,0,-600) rot=(1,0,0;3.14159rad)
  sketch-geometry (1):
    g0: Circle CenterX=673 CenterY=-6.3 CenterZ=0 NormalX=0 NormalY=0 NormalZ=1 AngleXU=0 Radius=4.025
  constraints (3):
    c: Diameter(g0) = 8.05
    c: DistanceX(g-1,g0) = 673
    c: Distance(g0,g-1) = 6.3
FEATURE [PartDesign::SubtractiveLoft] SubtractiveLoft003
  BaseFeature = -> AdditiveLoft003
  Closed = false
  Profile = -> Sketch014
  Refine = true
  Ruled = false
  Sections = -> [Sketch015]
  Suppressed = false
FEATURE [Sketcher::SketchObject] Sketch016
  ArcFitTolerance = 1e-06
  FullyConstrained = false
  MakeInternals = false
  Placement = pos=(600,0,-600) rot=(0,0,1;0rad)
  sketch-geometry (123):
    g0: BSplineCurve PolesCount=61 KnotsCount=61 Degree=3 IsPeriodic=1
    g1-g61: Circle [constr] x61 (B-spline internal-alignment scaffolding for g0; pole/knot coordinates omitted)
    g62-g122: GeomPoint [constr] x61 (B-spline internal-alignment scaffolding for g0; pole/knot coordinates omitted)
  constraints (123):
    c: InternalAlignment(g1,g0)
    c: Weight(g1) = 1
    c: InternalAlignment(g2,g0)
    c: Equal(g2,g1)
    c: InternalAlignment(g3,g0)
    c: Equal(g3,g1)
    c: InternalAlignment(g4,g0)
    c: Equal(g4,g1)
    c: InternalAlignment(g5,g0)
    c: Equal(g5,g1)
    c: InternalAlignment(g6,g0)
    c: Equal(g6,g1)
    c: InternalAlignment(g7,g0)
    c: Equal(g7,g1)
    c: InternalAlignment(g8,g0)
    c: Equal(g8,g1)
    c: InternalAlignment(g9,g0)
    c: Equal(g9,g1)
    c: InternalAlignment(g10,g0)
    c: Equal(g10,g1)
    c: InternalAlignment(g11,g0)
    c: Equal(g11,g1)
    c: InternalAlignment(g12,g0)
    c: Equal(g12,g1)
    c: InternalAlignment(g13,g0)
    c: Equal(g13,g1)
    c: InternalAlignment(g14,g0)
    c: Equal(g14,g1)
    c: InternalAlignment(g15,g0)
    c: Equal(g15,g1)
    c: InternalAlignment(g16,g0)
    c: Equal(g16,g1)
    c: InternalAlignment(g17,g0)
    c: Equal(g17,g1)
    c: InternalAlignment(g18,g0)
    c: Equal(g18,g1)
    c: InternalAlignment(g19,g0)
    c: Equal(g19,g1)
    c: InternalAlignment(g20,g0)
    c: Equal(g20,g1)
    c: InternalAlignment(g21,g0)
    c: Equal(g21,g1)
    c: InternalAlignment(g22,g0)
    c: Equal(g22,g1)
    c: InternalAlignment(g23,g0)
    c: Equal(g23,g1)
    c: InternalAlignment(g24,g0)
    c: Equal(g24,g1)
    c: InternalAlignment(g25,g0)
    c: Equal(g25,g1)
    c: InternalAlignment(g26,g0)
    c: Equal(g26,g1)
    c: InternalAlignment(g27,g0)
    c: Equal(g27,g1)
    c: InternalAlignment(g28,g0)
    c: Equal(g28,g1)
    c: InternalAlignment(g29,g0)
    c: Equal(g29,g1)
    c: InternalAlignment(g30,g0)
    c: Equal(g30,g1)
    c: InternalAlignment(g31,g0)
    c: Equal(g31,g1)
    c: InternalAlignment(g32,g0)
    c: Equal(g32,g1)
    c: InternalAlignment(g33,g0)
    c: Equal(g33,g1)
    c: InternalAlignment(g34,g0)
    c: Equal(g34,g1)
    c: InternalAlignment(g35,g0)
    c: Equal(g35,g1)
    c: InternalAlignment(g36,g0)
    c: Equal(g36,g1)
    c: InternalAlignment(g37,g0)
    c: Equal(g37,g1)
    c: InternalAlignment(g38,g0)
    c: Equal(g38,g1)
    c: InternalAlignment(g39,g0)
    c: Equal(g39,g1)
    c: InternalAlignment(g40,g0)
    c: Equal(g40,g1)
    c: InternalAlignment(g41,g0)
    c: Equal(g41,g1)
    c: InternalAlignment(g42,g0)
    c: Equal(g42,g1)
    c: InternalAlignment(g43,g0)
    c: Equal(g43,g1)
    c: InternalAlignment(g44,g0)
    c: Equal(g44,g1)
    c: InternalAlignment(g45,g0)
    c: Equal(g45,g1)
    c: InternalAlignment(g46,g0)
    c: Equal(g46,g1)
    c: InternalAlignment(g47,g0)
    c: Equal(g47,g1)
    c: InternalAlignment(g48,g0)
    c: Equal(g48,g1)
    c: InternalAlignment(g49,g0)
    c: Equal(g49,g1)
    c: InternalAlignment(g50,g0)
    c: Equal(g50,g1)
    c: InternalAlignment(g51,g0)
    c: Equal(g51,g1)
    c: InternalAlignment(g52,g0)
    c: Equal(g52,g1)
    c: InternalAlignment(g53,g0)
    c: Equal(g53,g1)
    c: InternalAlignment(g54,g0)
    c: Equal(g54,g1)
    c: InternalAlignment(g55,g0)
    c: Equal(g55,g1)
    c: InternalAlignment(g56,g0)
    c: Equal(g56,g1)
    c: InternalAlignment(g57,g0)
    c: Equal(g57,g1)
    c: InternalAlignment(g58,g0)
    c: Equal(g58,g1)
    c: InternalAlignment(g59,g0)
    c: Equal(g59,g1)
    c: InternalAlignment(g60,g0)
    c: Equal(g60,g1)
    c: InternalAlignment(g61,g0)
    c: Equal(g61,g1)
    c: InternalAlignment(g62-g122 -> g0) x61
FEATURE [Sketcher::SketchObject] Sketch017
  ArcFitTolerance = 1e-06
  FullyConstrained = false
  MakeInternals = false
  sketch-geometry (123):
    g0: BSplineCurve PolesCount=61 KnotsCount=61 Degree=3 IsPeriodic=1
    g1-g61: Circle [constr] x61 (B-spline internal-alignment scaffolding for g0; pole/knot coordinates omitted)
    g62-g122: GeomPoint [constr] x61 (B-spline internal-alignment scaffolding for g0; pole/knot coordinates omitted)
  constraints (123):
    c: InternalAlignment(g1,g0)
    c: Weight(g1) = 1
    c: InternalAlignment(g2,g0)
    c: Equal(g2,g1)
    c: InternalAlignment(g3,g0)
    c: Equal(g3,g1)
    c: InternalAlignment(g4,g0)
    c: Equal(g4,g1)
    c: InternalAlignment(g5,g0)
    c: Equal(g5,g1)
    c: InternalAlignment(g6,g0)
    c: Equal(g6,g1)
    c: InternalAlignment(g7,g0)
    c: Equal(g7,g1)
    c: InternalAlignment(g8,g0)
    c: Equal(g8,g1)
    c: InternalAlignment(g9,g0)
    c: Equal(g9,g1)
    c: InternalAlignment(g10,g0)
    c: Equal(g10,g1)
    c: InternalAlignment(g11,g0)
    c: Equal(g11,g1)
    c: InternalAlignment(g12,g0)
    c: Equal(g12,g1)
    c: InternalAlignment(g13,g0)
    c: Equal(g13,g1)
    c: InternalAlignment(g14,g0)
    c: Equal(g14,g1)
    c: InternalAlignment(g15,g0)
    c: Equal(g15,g1)
    c: InternalAlignment(g16,g0)
    c: Equal(g16,g1)
    c: InternalAlignment(g17,g0)
    c: Equal(g17,g1)
    c: InternalAlignment(g18,g0)
    c: Equal(g18,g1)
    c: InternalAlignment(g19,g0)
    c: Equal(g19,g1)
    c: InternalAlignment(g20,g0)
    c: Equal(g20,g1)
    c: InternalAlignment(g21,g0)
    c: Equal(g21,g1)
    c: InternalAlignment(g22,g0)
    c: Equal(g22,g1)
    c: InternalAlignment(g23,g0)
    c: Equal(g23,g1)
    c: InternalAlignment(g24,g0)
    c: Equal(g24,g1)
    c: InternalAlignment(g25,g0)
    c: Equal(g25,g1)
    c: InternalAlignment(g26,g0)
    c: Equal(g26,g1)
    c: InternalAlignment(g27,g0)
    c: Equal(g27,g1)
    c: InternalAlignment(g28,g0)
    c: Equal(g28,g1)
    c: InternalAlignment(g29,g0)
    c: Equal(g29,g1)
    c: InternalAlignment(g30,g0)
    c: Equal(g30,g1)
    c: InternalAlignment(g31,g0)
    c: Equal(g31,g1)
    c: InternalAlignment(g32,g0)
    c: Equal(g32,g1)
    c: InternalAlignment(g33,g0)
    c: Equal(g33,g1)
    c: InternalAlignment(g34,g0)
    c: Equal(g34,g1)
    c: InternalAlignment(g35,g0)
    c: Equal(g35,g1)
    c: InternalAlignment(g36,g0)
    c: Equal(g36,g1)
    c: InternalAlignment(g37,g0)
    c: Equal(g37,g1)
    c: InternalAlignment(g38,g0)
    c: Equal(g38,g1)
    c: InternalAlignment(g39,g0)
    c: Equal(g39,g1)
    c: InternalAlignment(g40,g0)
    c: Equal(g40,g1)
    c: InternalAlignment(g41,g0)
    c: Equal(g41,g1)
    c: InternalAlignment(g42,g0)
    c: Equal(g42,g1)
    c: InternalAlignment(g43,g0)
    c: Equal(g43,g1)
    c: InternalAlignment(g44,g0)
    c: Equal(g44,g1)
    c: InternalAlignment(g45,g0)
    c: Equal(g45,g1)
    c: InternalAlignment(g46,g0)
    c: Equal(g46,g1)
    c: InternalAlignment(g47,g0)
    c: Equal(g47,g1)
    c: InternalAlignment(g48,g0)
    c: Equal(g48,g1)
    c: InternalAlignment(g49,g0)
    c: Equal(g49,g1)
    c: InternalAlignment(g50,g0)
    c: Equal(g50,g1)
    c: InternalAlignment(g51,g0)
    c: Equal(g51,g1)
    c: InternalAlignment(g52,g0)
    c: Equal(g52,g1)
    c: InternalAlignment(g53,g0)
    c: Equal(g53,g1)
    c: InternalAlignment(g54,g0)
    c: Equal(g54,g1)
    c: InternalAlignment(g55,g0)
    c: Equal(g55,g1)
    c: InternalAlignment(g56,g0)
    c: Equal(g56,g1)
    c: InternalAlignment(g57,g0)
    c: Equal(g57,g1)
    c: InternalAlignment(g58,g0)
    c: Equal(g58,g1)
    c: InternalAlignment(g59,g0)
    c: Equal(g59,g1)
    c: InternalAlignment(g60,g0)
    c: Equal(g60,g1)
    c: InternalAlignment(g61,g0)
    c: Equal(g61,g1)
    c: InternalAlignment(g62-g122 -> g0) x61
FEATURE [PartDesign::AdditiveLoft] AdditiveLoft004
  Closed = false
  Profile = -> Sketch017
  Refine = true
  Ruled = false
  Sections = -> [Sketch016]
  Suppressed = false
FEATURE [Sketcher::SketchObject] Sketch018
  ArcFitTolerance = 1e-06
  AttachmentSupport = -> [AdditiveLoft004]
  FullyConstrained = true
  MakeInternals = false
  MapMode = 5
  sketch-geometry (1):
    g0: Circle CenterX=60 CenterY=8 CenterZ=0 NormalX=0 NormalY=0 NormalZ=1 AngleXU=0 Radius=4.025
  constraints (3):
    c: Diameter(g0) = 8.05
    c: DistanceX(g-1,g0) = 60
    c: Distance(g0,g-1) = 8
FEATURE [Sketcher::SketchObject] Sketch019
  ArcFitTolerance = 1e-06
  AttachmentSupport = -> [AdditiveLoft004]
  FullyConstrained = true
  MakeInternals = false
  MapMode = 5
  Placement = pos=(0,0,-600) rot=(1,0,0;3.14159rad)
  sketch-geometry (1):
    g0: Circle CenterX=673 CenterY=-6.3 CenterZ=0 NormalX=0 NormalY=0 NormalZ=1 AngleXU=0 Radius=4.025
  constraints (3):
    c: Diameter(g0) = 8.05
    c: DistanceX(g-1,g0) = 673
    c: Distance(g0,g-1) = 6.3
FEATURE [PartDesign::SubtractiveLoft] SubtractiveLoft004
  BaseFeature = -> AdditiveLoft004
  Closed = false
  Profile = -> Sketch018
  Refine = true
  Ruled = false
  Sections = -> [Sketch019]
  Suppressed = false
FEATURE [Sketcher::SketchObject] Sketch020
  ArcFitTolerance = 1e-06
  FullyConstrained = false
  MakeInternals = false
  Placement = pos=(600,0,-600) rot=(0,0,1;0rad)
  sketch-geometry (123):
    g0: BSplineCurve PolesCount=61 KnotsCount=61 Degree=3 IsPeriodic=1
    g1-g61: Circle [constr] x61 (B-spline internal-alignment scaffolding for g0; pole/knot coordinates omitted)
    g62-g122: GeomPoint [constr] x61 (B-spline internal-alignment scaffolding for g0; pole/knot coordinates omitted)
  constraints (123):
    c: InternalAlignment(g1,g0)
    c: Weight(g1) = 1
    c: InternalAlignment(g2,g0)
    c: Equal(g2,g1)
    c: InternalAlignment(g3,g0)
    c: Equal(g3,g1)
    c: InternalAlignment(g4,g0)
    c: Equal(g4,g1)
    c: InternalAlignment(g5,g0)
    c: Equal(g5,g1)
    c: InternalAlignment(g6,g0)
    c: Equal(g6,g1)
    c: InternalAlignment(g7,g0)
    c: Equal(g7,g1)
    c: InternalAlignment(g8,g0)
    c: Equal(g8,g1)
    c: InternalAlignment(g9,g0)
    c: Equal(g9,g1)
    c: InternalAlignment(g10,g0)
    c: Equal(g10,g1)
    c: InternalAlignment(g11,g0)
    c: Equal(g11,g1)
    c: InternalAlignment(g12,g0)
    c: Equal(g12,g1)
    c: InternalAlignment(g13,g0)
    c: Equal(g13,g1)
    c: InternalAlignment(g14,g0)
    c: Equal(g14,g1)
    c: InternalAlignment(g15,g0)
    c: Equal(g15,g1)
    c: InternalAlignment(g16,g0)
    c: Equal(g16,g1)
    c: InternalAlignment(g17,g0)
    c: Equal(g17,g1)
    c: InternalAlignment(g18,g0)
    c: Equal(g18,g1)
    c: InternalAlignment(g19,g0)
    c: Equal(g19,g1)
    c: InternalAlignment(g20,g0)
    c: Equal(g20,g1)
    c: InternalAlignment(g21,g0)
    c: Equal(g21,g1)
    c: InternalAlignment(g22,g0)
    c: Equal(g22,g1)
    c: InternalAlignment(g23,g0)
    c: Equal(g23,g1)
    c: InternalAlignment(g24,g0)
    c: Equal(g24,g1)
    c: InternalAlignment(g25,g0)
    c: Equal(g25,g1)
    c: InternalAlignment(g26,g0)
    c: Equal(g26,g1)
    c: InternalAlignment(g27,g0)
    c: Equal(g27,g1)
    c: InternalAlignment(g28,g0)
    c: Equal(g28,g1)
    c: InternalAlignment(g29,g0)
    c: Equal(g29,g1)
    c: InternalAlignment(g30,g0)
    c: Equal(g30,g1)
    c: InternalAlignment(g31,g0)
    c: Equal(g31,g1)
    c: InternalAlignment(g32,g0)
    c: Equal(g32,g1)
    c: InternalAlignment(g33,g0)
    c: Equal(g33,g1)
    c: InternalAlignment(g34,g0)
    c: Equal(g34,g1)
    c: InternalAlignment(g35,g0)
    c: Equal(g35,g1)
    c: InternalAlignment(g36,g0)
    c: Equal(g36,g1)
    c: InternalAlignment(g37,g0)
    c: Equal(g37,g1)
    c: InternalAlignment(g38,g0)
    c: Equal(g38,g1)
    c: InternalAlignment(g39,g0)
    c: Equal(g39,g1)
    c: InternalAlignment(g40,g0)
    c: Equal(g40,g1)
    c: InternalAlignment(g41,g0)
    c: Equal(g41,g1)
    c: InternalAlignment(g42,g0)
    c: Equal(g42,g1)
    c: InternalAlignment(g43,g0)
    c: Equal(g43,g1)
    c: InternalAlignment(g44,g0)
    c: Equal(g44,g1)
    c: InternalAlignment(g45,g0)
    c: Equal(g45,g1)
    c: InternalAlignment(g46,g0)
    c: Equal(g46,g1)
    c: InternalAlignment(g47,g0)
    c: Equal(g47,g1)
    c: InternalAlignment(g48,g0)
    c: Equal(g48,g1)
    c: InternalAlignment(g49,g0)
    c: Equal(g49,g1)
    c: InternalAlignment(g50,g0)
    c: Equal(g50,g1)
    c: InternalAlignment(g51,g0)
    c: Equal(g51,g1)
    c: InternalAlignment(g52,g0)
    c: Equal(g52,g1)
    c: InternalAlignment(g53,g0)
    c: Equal(g53,g1)
    c: InternalAlignment(g54,g0)
    c: Equal(g54,g1)
    c: InternalAlignment(g55,g0)
    c: Equal(g55,g1)
    c: InternalAlignment(g56,g0)
    c: Equal(g56,g1)
    c: InternalAlignment(g57,g0)
    c: Equal(g57,g1)
    c: InternalAlignment(g58,g0)
    c: Equal(g58,g1)
    c: InternalAlignment(g59,g0)
    c: Equal(g59,g1)
    c: InternalAlignment(g60,g0)
    c: Equal(g60,g1)
    c: InternalAlignment(g61,g0)
    c: Equal(g61,g1)
    c: InternalAlignment(g62-g122 -> g0) x61
FEATURE [Sketcher::SketchObject] Sketch021
  ArcFitTolerance = 1e-06
  FullyConstrained = false
  MakeInternals = false
  sketch-geometry (123):
    g0: BSplineCurve PolesCount=61 KnotsCount=61 Degree=3 IsPeriodic=1
    g1-g61: Circle [constr] x61 (B-spline internal-alignment scaffolding for g0; pole/knot coordinates omitted)
    g62-g122: GeomPoint [constr] x61 (B-spline internal-alignment scaffolding for g0; pole/knot coordinates omitted)
  constraints (123):
    c: InternalAlignment(g1,g0)
    c: Weight(g1) = 1
    c: InternalAlignment(g2,g0)
    c: Equal(g2,g1)
    c: InternalAlignment(g3,g0)
    c: Equal(g3,g1)
    c: InternalAlignment(g4,g0)
    c: Equal(g4,g1)
    c: InternalAlignment(g5,g0)
    c: Equal(g5,g1)
    c: InternalAlignment(g6,g0)
    c: Equal(g6,g1)
    c: InternalAlignment(g7,g0)
    c: Equal(g7,g1)
    c: InternalAlignment(g8,g0)
    c: Equal(g8,g1)
    c: InternalAlignment(g9,g0)
    c: Equal(g9,g1)
    c: InternalAlignment(g10,g0)
    c: Equal(g10,g1)
    c: InternalAlignment(g11,g0)
    c: Equal(g11,g1)
    c: InternalAlignment(g12,g0)
    c: Equal(g12,g1)
    c: InternalAlignment(g13,g0)
    c: Equal(g13,g1)
    c: InternalAlignment(g14,g0)
    c: Equal(g14,g1)
    c: InternalAlignment(g15,g0)
    c: Equal(g15,g1)
    c: InternalAlignment(g16,g0)
    c: Equal(g16,g1)
    c: InternalAlignment(g17,g0)
    c: Equal(g17,g1)
    c: InternalAlignment(g18,g0)
    c: Equal(g18,g1)
    c: InternalAlignment(g19,g0)
    c: Equal(g19,g1)
    c: InternalAlignment(g20,g0)
    c: Equal(g20,g1)
    c: InternalAlignment(g21,g0)
    c: Equal(g21,g1)
    c: InternalAlignment(g22,g0)
    c: Equal(g22,g1)
    c: InternalAlignment(g23,g0)
    c: Equal(g23,g1)
    c: InternalAlignment(g24,g0)
    c: Equal(g24,g1)
    c: InternalAlignment(g25,g0)
    c: Equal(g25,g1)
    c: InternalAlignment(g26,g0)
    c: Equal(g26,g1)
    c: InternalAlignment(g27,g0)
    c: Equal(g27,g1)
    c: InternalAlignment(g28,g0)
    c: Equal(g28,g1)
    c: InternalAlignment(g29,g0)
    c: Equal(g29,g1)
    c: InternalAlignment(g30,g0)
    c: Equal(g30,g1)
    c: InternalAlignment(g31,g0)
    c: Equal(g31,g1)
    c: InternalAlignment(g32,g0)
    c: Equal(g32,g1)
    c: InternalAlignment(g33,g0)
    c: Equal(g33,g1)
    c: InternalAlignment(g34,g0)
    c: Equal(g34,g1)
    c: InternalAlignment(g35,g0)
    c: Equal(g35,g1)
    c: InternalAlignment(g36,g0)
    c: Equal(g36,g1)
    c: InternalAlignment(g37,g0)
    c: Equal(g37,g1)
    c: InternalAlignment(g38,g0)
    c: Equal(g38,g1)
    c: InternalAlignment(g39,g0)
    c: Equal(g39,g1)
    c: InternalAlignment(g40,g0)
    c: Equal(g40,g1)
    c: InternalAlignment(g41,g0)
    c: Equal(g41,g1)
    c: InternalAlignment(g42,g0)
    c: Equal(g42,g1)
    c: InternalAlignment(g43,g0)
    c: Equal(g43,g1)
    c: InternalAlignment(g44,g0)
    c: Equal(g44,g1)
    c: InternalAlignment(g45,g0)
    c: Equal(g45,g1)
    c: InternalAlignment(g46,g0)
    c: Equal(g46,g1)
    c: InternalAlignment(g47,g0)
    c: Equal(g47,g1)
    c: InternalAlignment(g48,g0)
    c: Equal(g48,g1)
    c: InternalAlignment(g49,g0)
    c: Equal(g49,g1)
    c: InternalAlignment(g50,g0)
    c: Equal(g50,g1)
    c: InternalAlignment(g51,g0)
    c: Equal(g51,g1)
    c: InternalAlignment(g52,g0)
    c: Equal(g52,g1)
    c: InternalAlignment(g53,g0)
    c: Equal(g53,g1)
    c: InternalAlignment(g54,g0)
    c: Equal(g54,g1)
    c: InternalAlignment(g55,g0)
    c: Equal(g55,g1)
    c: InternalAlignment(g56,g0)
    c: Equal(g56,g1)
    c: InternalAlignment(g57,g0)
    c: Equal(g57,g1)
    c: InternalAlignment(g58,g0)
    c: Equal(g58,g1)
    c: InternalAlignment(g59,g0)
    c: Equal(g59,g1)
    c: InternalAlignment(g60,g0)
    c: Equal(g60,g1)
    c: InternalAlignment(g61,g0)
    c: Equal(g61,g1)
    c: InternalAlignment(g62-g122 -> g0) x61
FEATURE [PartDesign::AdditiveLoft] AdditiveLoft005
  Closed = false
  Profile = -> Sketch021
  Refine = true
  Ruled = false
  Sections = -> [Sketch020]
  Suppressed = false
FEATURE [Sketcher::SketchObject] Sketch022
  ArcFitTolerance = 1e-06
  AttachmentSupport = -> [AdditiveLoft005]
  FullyConstrained = true
  MakeInternals = false
  MapMode = 5
  sketch-geometry (1):
    g0: Circle CenterX=60 CenterY=8 CenterZ=0 NormalX=0 NormalY=0 NormalZ=1 AngleXU=0 Radius=4.025
  constraints (3):
    c: Diameter(g0) = 8.05
    c: DistanceX(g-1,g0) = 60
    c: Distance(g0,g-1) = 8
FEATURE [Sketcher::SketchObject] Sketch023
  ArcFitTolerance = 1e-06
  AttachmentSupport = -> [AdditiveLoft005]
  FullyConstrained = true
  MakeInternals = false
  MapMode = 5
  Placement = pos=(0,0,-600) rot=(1,0,0;3.14159rad)
  sketch-geometry (1):
    g0: Circle CenterX=673 CenterY=-6.3 CenterZ=0 NormalX=0 NormalY=0 NormalZ=1 AngleXU=0 Radius=4.025
  constraints (3):
    c: Diameter(g0) = 8.05
    c: DistanceX(g-1,g0) = 673
    c: Distance(g0,g-1) = 6.3
FEATURE [PartDesign::SubtractiveLoft] SubtractiveLoft005
  BaseFeature = -> AdditiveLoft005
  Closed = false
  Profile = -> Sketch022
  Refine = true
  Ruled = false
  Sections = -> [Sketch023]
  Suppressed = false
FEATURE [Sketcher::SketchObject] Sketch024
  ArcFitTolerance = 1e-06
  FullyConstrained = false
  MakeInternals = false
  Placement = pos=(600,0,-600) rot=(0,0,1;0rad)
  sketch-geometry (123):
    g0: BSplineCurve PolesCount=61 KnotsCount=61 Degree=3 IsPeriodic=1
    g1-g61: Circle [constr] x61 (B-spline internal-alignment scaffolding for g0; pole/knot coordinates omitted)
    g62-g122: GeomPoint [constr] x61 (B-spline internal-alignment scaffolding for g0; pole/knot coordinates omitted)
  constraints (123):
    c: InternalAlignment(g1,g0)
    c: Weight(g1) = 1
    c: InternalAlignment(g2,g0)
    c: Equal(g2,g1)
    c: InternalAlignment(g3,g0)
    c: Equal(g3,g1)
    c: InternalAlignment(g4,g0)
    c: Equal(g4,g1)
    c: InternalAlignment(g5,g0)
    c: Equal(g5,g1)
    c: InternalAlignment(g6,g0)
    c: Equal(g6,g1)
    c: InternalAlignment(g7,g0)
    c: Equal(g7,g1)
    c: InternalAlignment(g8,g0)
    c: Equal(g8,g1)
    c: InternalAlignment(g9,g0)
    c: Equal(g9,g1)
    c: InternalAlignment(g10,g0)
    c: Equal(g10,g1)
    c: InternalAlignment(g11,g0)
    c: Equal(g11,g1)
    c: InternalAlignment(g12,g0)
    c: Equal(g12,g1)
    c: InternalAlignment(g13,g0)
    c: Equal(g13,g1)
    c: InternalAlignment(g14,g0)
    c: Equal(g14,g1)
    c: InternalAlignment(g15,g0)
    c: Equal(g15,g1)
    c: InternalAlignment(g16,g0)
    c: Equal(g16,g1)
    c: InternalAlignment(g17,g0)
    c: Equal(g17,g1)
    c: InternalAlignment(g18,g0)
    c: Equal(g18,g1)
    c: InternalAlignment(g19,g0)
    c: Equal(g19,g1)
    c: InternalAlignment(g20,g0)
    c: Equal(g20,g1)
    c: InternalAlignment(g21,g0)
    c: Equal(g21,g1)
    c: InternalAlignment(g22,g0)
    c: Equal(g22,g1)
    c: InternalAlignment(g23,g0)
    c: Equal(g23,g1)
    c: InternalAlignment(g24,g0)
    c: Equal(g24,g1)
    c: InternalAlignment(g25,g0)
    c: Equal(g25,g1)
    c: InternalAlignment(g26,g0)
    c: Equal(g26,g1)
    c: InternalAlignment(g27,g0)
    c: Equal(g27,g1)
    c: InternalAlignment(g28,g0)
    c: Equal(g28,g1)
    c: InternalAlignment(g29,g0)
    c: Equal(g29,g1)
    c: InternalAlignment(g30,g0)
    c: Equal(g30,g1)
    c: InternalAlignment(g31,g0)
    c: Equal(g31,g1)
    c: InternalAlignment(g32,g0)
    c: Equal(g32,g1)
    c: InternalAlignment(g33,g0)
    c: Equal(g33,g1)
    c: InternalAlignment(g34,g0)
    c: Equal(g34,g1)
    c: InternalAlignment(g35,g0)
    c: Equal(g35,g1)
    c: InternalAlignment(g36,g0)
    c: Equal(g36,g1)
    c: InternalAlignment(g37,g0)
    c: Equal(g37,g1)
    c: InternalAlignment(g38,g0)
    c: Equal(g38,g1)
    c: InternalAlignment(g39,g0)
    c: Equal(g39,g1)
    c: InternalAlignment(g40,g0)
    c: Equal(g40,g1)
    c: InternalAlignment(g41,g0)
    c: Equal(g41,g1)
    c: InternalAlignment(g42,g0)
    c: Equal(g42,g1)
    c: InternalAlignment(g43,g0)
    c: Equal(g43,g1)
    c: InternalAlignment(g44,g0)
    c: Equal(g44,g1)
    c: InternalAlignment(g45,g0)
    c: Equal(g45,g1)
    c: InternalAlignment(g46,g0)
    c: Equal(g46,g1)
    c: InternalAlignment(g47,g0)
    c: Equal(g47,g1)
    c: InternalAlignment(g48,g0)
    c: Equal(g48,g1)
    c: InternalAlignment(g49,g0)
    c: Equal(g49,g1)
    c: InternalAlignment(g50,g0)
    c: Equal(g50,g1)
    c: InternalAlignment(g51,g0)
    c: Equal(g51,g1)
    c: InternalAlignment(g52,g0)
    c: Equal(g52,g1)
    c: InternalAlignment(g53,g0)
    c: Equal(g53,g1)
    c: InternalAlignment(g54,g0)
    c: Equal(g54,g1)
    c: InternalAlignment(g55,g0)
    c: Equal(g55,g1)
    c: InternalAlignment(g56,g0)
    c: Equal(g56,g1)
    c: InternalAlignment(g57,g0)
    c: Equal(g57,g1)
    c: InternalAlignment(g58,g0)
    c: Equal(g58,g1)
    c: InternalAlignment(g59,g0)
    c: Equal(g59,g1)
    c: InternalAlignment(g60,g0)
    c: Equal(g60,g1)
    c: InternalAlignment(g61,g0)
    c: Equal(g61,g1)
    c: InternalAlignment(g62-g122 -> g0) x61
FEATURE [Sketcher::SketchObject] Sketch025
  ArcFitTolerance = 1e-06
  FullyConstrained = false
  MakeInternals = false
  sketch-geometry (123):
    g0: BSplineCurve PolesCount=61 KnotsCount=61 Degree=3 IsPeriodic=1
    g1-g61: Circle [constr] x61 (B-spline internal-alignment scaffolding for g0; pole/knot coordinates omitted)
    g62-g122: GeomPoint [constr] x61 (B-spline internal-alignment scaffolding for g0; pole/knot coordinates omitted)
  constraints (123):
    c: InternalAlignment(g1,g0)
    c: Weight(g1) = 1
    c: InternalAlignment(g2,g0)
    c: Equal(g2,g1)
    c: InternalAlignment(g3,g0)
    c: Equal(g3,g1)
    c: InternalAlignment(g4,g0)
    c: Equal(g4,g1)
    c: InternalAlignment(g5,g0)
    c: Equal(g5,g1)
    c: InternalAlignment(g6,g0)
    c: Equal(g6,g1)
    c: InternalAlignment(g7,g0)
    c: Equal(g7,g1)
    c: InternalAlignment(g8,g0)
    c: Equal(g8,g1)
    c: InternalAlignment(g9,g0)
    c: Equal(g9,g1)
    c: InternalAlignment(g10,g0)
    c: Equal(g10,g1)
    c: InternalAlignment(g11,g0)
    c: Equal(g11,g1)
    c: InternalAlignment(g12,g0)
    c: Equal(g12,g1)
    c: InternalAlignment(g13,g0)
    c: Equal(g13,g1)
    c: InternalAlignment(g14,g0)
    c: Equal(g14,g1)
    c: InternalAlignment(g15,g0)
    c: Equal(g15,g1)
    c: InternalAlignment(g16,g0)
    c: Equal(g16,g1)
    c: InternalAlignment(g17,g0)
    c: Equal(g17,g1)
    c: InternalAlignment(g18,g0)
    c: Equal(g18,g1)
    c: InternalAlignment(g19,g0)
    c: Equal(g19,g1)
    c: InternalAlignment(g20,g0)
    c: Equal(g20,g1)
    c: InternalAlignment(g21,g0)
    c: Equal(g21,g1)
    c: InternalAlignment(g22,g0)
    c: Equal(g22,g1)
    c: InternalAlignment(g23,g0)
    c: Equal(g23,g1)
    c: InternalAlignment(g24,g0)
    c: Equal(g24,g1)
    c: InternalAlignment(g25,g0)
    c: Equal(g25,g1)
    c: InternalAlignment(g26,g0)
    c: Equal(g26,g1)
    c: InternalAlignment(g27,g0)
    c: Equal(g27,g1)
    c: InternalAlignment(g28,g0)
    c: Equal(g28,g1)
    c: InternalAlignment(g29,g0)
    c: Equal(g29,g1)
    c: InternalAlignment(g30,g0)
    c: Equal(g30,g1)
    c: InternalAlignment(g31,g0)
    c: Equal(g31,g1)
    c: InternalAlignment(g32,g0)
    c: Equal(g32,g1)
    c: InternalAlignment(g33,g0)
    c: Equal(g33,g1)
    c: InternalAlignment(g34,g0)
    c: Equal(g34,g1)
    c: InternalAlignment(g35,g0)
    c: Equal(g35,g1)
    c: InternalAlignment(g36,g0)
    c: Equal(g36,g1)
    c: InternalAlignment(g37,g0)
    c: Equal(g37,g1)
    c: InternalAlignment(g38,g0)
    c: Equal(g38,g1)
    c: InternalAlignment(g39,g0)
    c: Equal(g39,g1)
    c: InternalAlignment(g40,g0)
    c: Equal(g40,g1)
    c: InternalAlignment(g41,g0)
    c: Equal(g41,g1)
    c: InternalAlignment(g42,g0)
    c: Equal(g42,g1)
    c: InternalAlignment(g43,g0)
    c: Equal(g43,g1)
    c: InternalAlignment(g44,g0)
    c: Equal(g44,g1)
    c: InternalAlignment(g45,g0)
    c: Equal(g45,g1)
    c: InternalAlignment(g46,g0)
    c: Equal(g46,g1)
    c: InternalAlignment(g47,g0)
    c: Equal(g47,g1)
    c: InternalAlignment(g48,g0)
    c: Equal(g48,g1)
    c: InternalAlignment(g49,g0)
    c: Equal(g49,g1)
    c: InternalAlignment(g50,g0)
    c: Equal(g50,g1)
    c: InternalAlignment(g51,g0)
    c: Equal(g51,g1)
    c: InternalAlignment(g52,g0)
    c: Equal(g52,g1)
    c: InternalAlignment(g53,g0)
    c: Equal(g53,g1)
    c: InternalAlignment(g54,g0)
    c: Equal(g54,g1)
    c: InternalAlignment(g55,g0)
    c: Equal(g55,g1)
    c: InternalAlignment(g56,g0)
    c: Equal(g56,g1)
    c: InternalAlignment(g57,g0)
    c: Equal(g57,g1)
    c: InternalAlignment(g58,g0)
    c: Equal(g58,g1)
    c: InternalAlignment(g59,g0)
    c: Equal(g59,g1)
    c: InternalAlignment(g60,g0)
    c: Equal(g60,g1)
    c: InternalAlignment(g61,g0)
    c: Equal(g61,g1)
    c: InternalAlignment(g62-g122 -> g0) x61
FEATURE [PartDesign::AdditiveLoft] AdditiveLoft006
  Closed = false
  Profile = -> Sketch025
  Refine = true
  Ruled = false
  Sections = -> [Sketch024]
  Suppressed = false
FEATURE [Sketcher::SketchObject] Sketch028
  ArcFitTolerance = 1e-06
  AttachmentSupport = -> [SubtractiveLoft]
  FullyConstrained = false
  MakeInternals = false
  MapMode = 5
  Placement = pos=(0,0,-600) rot=(1,0,0;3.14159rad)
  sketch-geometry (4):
    g0: LineSegment StartX=-361.684 StartY=239.009 StartZ=0 EndX=-361.684 EndY=-272.444 EndZ=0
    g1: LineSegment StartX=-361.684 StartY=-272.444 StartZ=0 EndX=1190.03 EndY=-272.444 EndZ=0
    g2: LineSegment StartX=1190.03 StartY=-272.444 StartZ=0 EndX=1190.03 EndY=239.009 EndZ=0
    g3: LineSegment StartX=1190.03 StartY=239.009 StartZ=0 EndX=-361.684 EndY=239.009 EndZ=0
  constraints (8):
    c: Coincident(g0,g1)
    c: Coincident(g1,g2)
    c: Coincident(g2,g3)
    c: Coincident(g3,g0)
    c: Vertical(g0)
    c: Vertical(g2)
    c: Horizontal(g1)
    c: Horizontal(g3)
FEATURE [PartDesign::Pocket] Pocket
  BaseFeature = -> SubtractiveLoft
  Direction = (0,0,1)
  Length = 590
  Length2 = 5
  Profile = -> Sketch028
  ReferenceAxis = -> Sketch028 [N_Axis]
  Refine = true
  Suppressed = false
  Type = 0
FEATURE [PartDesign::Body] Body
  AllowCompound = false
  Group = -> [Sketch,Sketch001,AdditiveLoft,Sketch002,Sketch003,SubtractiveLoft,Sketch028,Pocket]
  Origin = -> Origin
  Tip = -> Pocket
FEATURE [Sketcher::SketchObject] Sketch029
  ArcFitTolerance = 1e-06
  AttachmentSupport = -> [SubtractiveLoft001]
  FullyConstrained = false
  MakeInternals = false
  MapMode = 5
  sketch-geometry (4):
    g0: LineSegment StartX=-183.305 StartY=225.71 StartZ=0 EndX=-183.305 EndY=-177.33 EndZ=0
    g1: LineSegment StartX=-183.305 StartY=-177.33 StartZ=0 EndX=692.316 EndY=-177.33 EndZ=0
    g2: LineSegment StartX=692.316 StartY=-177.33 StartZ=0 EndX=692.316 EndY=225.71 EndZ=0
    g3: LineSegment StartX=692.316 StartY=225.71 StartZ=0 EndX=-183.305 EndY=225.71 EndZ=0
  constraints (8):
    c: Coincident(g0,g1)
    c: Coincident(g1,g2)
    c: Coincident(g2,g3)
    c: Coincident(g3,g0)
    c: Vertical(g0)
    c: Vertical(g2)
    c: Horizontal(g1)
    c: Horizontal(g3)
FEATURE [PartDesign::Pocket] Pocket001
  BaseFeature = -> SubtractiveLoft001
  Direction = (0,0,-1)
  Length = 100
  Length2 = 5
  Profile = -> Sketch029
  ReferenceAxis = -> Sketch029 [N_Axis]
  Refine = true
  Suppressed = false
  Type = 0
FEATURE [Sketcher::SketchObject] Sketch030
  ArcFitTolerance = 1e-06
  AttachmentSupport = -> [Pocket001]
  FullyConstrained = false
  MakeInternals = false
  MapMode = 5
  Placement = pos=(0,0,-600) rot=(1,0,0;3.14159rad)
  sketch-geometry (4):
    g0: LineSegment StartX=59.9757 StartY=189.035 StartZ=0 EndX=59.9757 EndY=-249.15 EndZ=0
    g1: LineSegment StartX=59.9757 StartY=-249.15 StartZ=0 EndX=1132.26 EndY=-249.15 EndZ=0
    g2: LineSegment StartX=1132.26 StartY=-249.15 StartZ=0 EndX=1132.26 EndY=189.035 EndZ=0
    g3: LineSegment StartX=1132.26 StartY=189.035 StartZ=0 EndX=59.9757 EndY=189.035 EndZ=0
  constraints (8):
    c: Coincident(g0,g1)
    c: Coincident(g1,g2)
    c: Coincident(g2,g3)
    c: Coincident(g3,g0)
    c: Vertical(g0)
    c: Vertical(g2)
    c: Horizontal(g1)
    c: Horizontal(g3)
FEATURE [PartDesign::Pocket] Pocket002
  BaseFeature = -> Pocket001
  Direction = (0,0,1)
  Length = 490
  Length2 = 5
  Profile = -> Sketch030
  ReferenceAxis = -> Sketch030 [N_Axis]
  Refine = true
  Suppressed = false
  Type = 0
FEATURE [PartDesign::Body] Body001
  AllowCompound = false
  Group = -> [Sketch004,Sketch005,AdditiveLoft001,Sketch006,Sketch007,SubtractiveLoft001,Sketch029,Pocket001,Sketch030,Pocket002]
  Origin = -> Origin001
  Tip = -> Pocket002
FEATURE [Sketcher::SketchObject] Sketch031
  ArcFitTolerance = 1e-06
  AttachmentSupport = -> [SubtractiveLoft002]
  FullyConstrained = false
  MakeInternals = false
  MapMode = 5
  sketch-geometry (4):
    g0: LineSegment StartX=-293.686 StartY=252.665 StartZ=0 EndX=-293.686 EndY=-208.556 EndZ=0
    g1: LineSegment StartX=-293.686 StartY=-208.556 StartZ=0 EndX=1201.4 EndY=-208.556 EndZ=0
    g2: LineSegment StartX=1201.4 StartY=-208.556 StartZ=0 EndX=1201.4 EndY=252.665 EndZ=0
    g3: LineSegment StartX=1201.4 StartY=252.665 StartZ=0 EndX=-293.686 EndY=252.665 EndZ=0
  constraints (8):
    c: Coincident(g0,g1)
    c: Coincident(g1,g2)
    c: Coincident(g2,g3)
    c: Coincident(g3,g0)
    c: Vertical(g0)
    c: Vertical(g2)
    c: Horizontal(g1)
    c: Horizontal(g3)
FEATURE [PartDesign::Pocket] Pocket003
  BaseFeature = -> SubtractiveLoft002
  Direction = (0,0,-1)
  Length = 200
  Length2 = 5
  Profile = -> Sketch031
  ReferenceAxis = -> Sketch031 [N_Axis]
  Refine = true
  Suppressed = false
  Type = 0
FEATURE [Sketcher::SketchObject] Sketch032
  ArcFitTolerance = 1e-06
  AttachmentSupport = -> [Pocket003]
  FullyConstrained = false
  MakeInternals = false
  MapMode = 5
  Placement = pos=(0,0,-600) rot=(1,0,0;3.14159rad)
  sketch-geometry (4):
    g0: LineSegment StartX=116.709 StartY=135.532 StartZ=0 EndX=116.709 EndY=-144.854 EndZ=0
    g1: LineSegment StartX=116.709 StartY=-144.854 StartZ=0 EndX=1093.95 EndY=-144.854 EndZ=0
    g2: LineSegment StartX=1093.95 StartY=-144.854 StartZ=0 EndX=1093.95 EndY=135.532 EndZ=0
    g3: LineSegment StartX=1093.95 StartY=135.532 StartZ=0 EndX=116.709 EndY=135.532 EndZ=0
  constraints (8):
    c: Coincident(g0,g1)
    c: Coincident(g1,g2)
    c: Coincident(g2,g3)
    c: Coincident(g3,g0)
    c: Vertical(g0)
    c: Vertical(g2)
    c: Horizontal(g1)
    c: Horizontal(g3)
FEATURE [PartDesign::Pocket] Pocket004
  BaseFeature = -> Pocket003
  Direction = (0,0,1)
  Length = 390
  Length2 = 5
  Profile = -> Sketch032
  ReferenceAxis = -> Sketch032 [N_Axis]
  Refine = true
  Suppressed = false
  Type = 0
FEATURE [PartDesign::Body] Body002
  AllowCompound = false
  Group = -> [Sketch008,Sketch009,AdditiveLoft002,Sketch010,Sketch011,SubtractiveLoft002,Sketch031,Pocket003,Sketch032,Pocket004]
  Origin = -> Origin002
  Tip = -> Pocket004
FEATURE [Sketcher::SketchObject] Sketch033
  ArcFitTolerance = 1e-06
  AttachmentSupport = -> [SubtractiveLoft003]
  FullyConstrained = false
  MakeInternals = false
  MapMode = 5
  sketch-geometry (4):
    g0: LineSegment StartX=-354.898 StartY=261.164 StartZ=0 EndX=-354.898 EndY=-258.668 EndZ=0
    g1: LineSegment StartX=-354.898 StartY=-258.668 StartZ=0 EndX=1040.62 EndY=-258.668 EndZ=0
    g2: LineSegment StartX=1040.62 StartY=-258.668 StartZ=0 EndX=1040.62 EndY=261.164 EndZ=0
    g3: LineSegment StartX=1040.62 StartY=261.164 StartZ=0 EndX=-354.898 EndY=261.164 EndZ=0
  constraints (8):
    c: Coincident(g0,g1)
    c: Coincident(g1,g2)
    c: Coincident(g2,g3)
    c: Coincident(g3,g0)
    c: Vertical(g0)
    c: Vertical(g2)
    c: Horizontal(g1)
    c: Horizontal(g3)
FEATURE [PartDesign::Pocket] Pocket005
  BaseFeature = -> SubtractiveLoft003
  Direction = (0,0,-1)
  Length = 300
  Length2 = 5
  Profile = -> Sketch033
  ReferenceAxis = -> Sketch033 [N_Axis]
  Refine = true
  Suppressed = false
  Type = 0
FEATURE [Sketcher::SketchObject] Sketch034
  ArcFitTolerance = 1e-06
  AttachmentSupport = -> [Pocket005]
  FullyConstrained = false
  MakeInternals = false
  MapMode = 5
  Placement = pos=(0,0,-600) rot=(1,0,0;3.14159rad)
  sketch-geometry (4):
    g0: LineSegment StartX=233.866 StartY=117.223 StartZ=0 EndX=233.866 EndY=-142.996 EndZ=0
    g1: LineSegment StartX=233.866 StartY=-142.996 StartZ=0 EndX=1170.8 EndY=-142.996 EndZ=0
    g2: LineSegment StartX=1170.8 StartY=-142.996 StartZ=0 EndX=1170.8 EndY=117.223 EndZ=0
    g3: LineSegment StartX=1170.8 StartY=117.223 StartZ=0 EndX=233.866 EndY=117.223 EndZ=0
  constraints (8):
    c: Coincident(g0,g1)
    c: Coincident(g1,g2)
    c: Coincident(g2,g3)
    c: Coincident(g3,g0)
    c: Vertical(g0)
    c: Vertical(g2)
    c: Horizontal(g1)
    c: Horizontal(g3)
FEATURE [PartDesign::Pocket] Pocket006
  BaseFeature = -> Pocket005
  Direction = (0,0,1)
  Length = 290
  Length2 = 5
  Profile = -> Sketch034
  ReferenceAxis = -> Sketch034 [N_Axis]
  Refine = true
  Suppressed = false
  Type = 0
FEATURE [PartDesign::Body] Body003
  AllowCompound = false
  Group = -> [Sketch012,Sketch013,AdditiveLoft003,Sketch014,Sketch015,SubtractiveLoft003,Sketch033,Pocket005,Sketch034,Pocket006]
  Origin = -> Origin003
  Tip = -> Pocket006
FEATURE [Sketcher::SketchObject] Sketch035
  ArcFitTolerance = 1e-06
  AttachmentSupport = -> [SubtractiveLoft004]
  FullyConstrained = false
  MakeInternals = false
  MapMode = 5
  sketch-geometry (4):
    g0: LineSegment StartX=-152.611 StartY=166.646 StartZ=0 EndX=-152.611 EndY=-181.325 EndZ=0
    g1: LineSegment StartX=-152.611 StartY=-181.325 StartZ=0 EndX=998.16 EndY=-181.325 EndZ=0
    g2: LineSegment StartX=998.16 StartY=-181.325 StartZ=0 EndX=998.16 EndY=166.646 EndZ=0
    g3: LineSegment StartX=998.16 StartY=166.646 StartZ=0 EndX=-152.611 EndY=166.646 EndZ=0
  constraints (8):
    c: Coincident(g0,g1)
    c: Coincident(g1,g2)
    c: Coincident(g2,g3)
    c: Coincident(g3,g0)
    c: Vertical(g0)
    c: Vertical(g2)
    c: Horizontal(g1)
    c: Horizontal(g3)
FEATURE [PartDesign::Pocket] Pocket007
  BaseFeature = -> SubtractiveLoft004
  Direction = (0,0,-1)
  Length = 400
  Length2 = 5
  Profile = -> Sketch035
  ReferenceAxis = -> Sketch035 [N_Axis]
  Refine = true
  Suppressed = false
  Type = 0
FEATURE [Sketcher::SketchObject] Sketch036
  ArcFitTolerance = 1e-06
  AttachmentSupport = -> [Pocket007]
  FullyConstrained = false
  MakeInternals = false
  MapMode = 5
  Placement = pos=(0,0,-600) rot=(1,0,0;3.14159rad)
  sketch-geometry (4):
    g0: LineSegment StartX=317.939 StartY=104.419 StartZ=0 EndX=317.939 EndY=-133.954 EndZ=0
    g1: LineSegment StartX=317.939 StartY=-133.954 StartZ=0 EndX=1060.46 EndY=-133.954 EndZ=0
    g2: LineSegment StartX=1060.46 StartY=-133.954 StartZ=0 EndX=1060.46 EndY=104.419 EndZ=0
    g3: LineSegment StartX=1060.46 StartY=104.419 StartZ=0 EndX=317.939 EndY=104.419 EndZ=0
  constraints (8):
    c: Coincident(g0,g1)
    c: Coincident(g1,g2)
    c: Coincident(g2,g3)
    c: Coincident(g3,g0)
    c: Vertical(g0)
    c: Vertical(g2)
    c: Horizontal(g1)
    c: Horizontal(g3)
FEATURE [PartDesign::Pocket] Pocket008
  BaseFeature = -> Pocket007
  Direction = (0,0,1)
  Length = 190
  Length2 = 5
  Profile = -> Sketch036
  ReferenceAxis = -> Sketch036 [N_Axis]
  Refine = true
  Suppressed = false
  Type = 0
FEATURE [PartDesign::Body] Body004
  AllowCompound = false
  Group = -> [Sketch016,Sketch017,AdditiveLoft004,Sketch018,Sketch019,SubtractiveLoft004,Sketch035,Pocket007,Sketch036,Pocket008]
  Origin = -> Origin004
  Tip = -> Pocket008
FEATURE [Sketcher::SketchObject] Sketch037
  ArcFitTolerance = 1e-06
  AttachmentSupport = -> [SubtractiveLoft005]
  FullyConstrained = false
  MakeInternals = false
  MapMode = 5
  sketch-geometry (4):
    g0: LineSegment StartX=-768.693 StartY=349.519 StartZ=0 EndX=-768.693 EndY=-271.212 EndZ=0
    g1: LineSegment StartX=-768.693 StartY=-271.212 StartZ=0 EndX=1592.75 EndY=-271.212 EndZ=0
    g2: LineSegment StartX=1592.75 StartY=-271.212 StartZ=0 EndX=1592.75 EndY=349.519 EndZ=0
    g3: LineSegment StartX=1592.75 StartY=349.519 StartZ=0 EndX=-768.693 EndY=349.519 EndZ=0
  constraints (8):
    c: Coincident(g0,g1)
    c: Coincident(g1,g2)
    c: Coincident(g2,g3)
    c: Coincident(g3,g0)
    c: Vertical(g0)
    c: Vertical(g2)
    c: Horizontal(g1)
    c: Horizontal(g3)
FEATURE [PartDesign::Pocket] Pocket009
  BaseFeature = -> SubtractiveLoft005
  Direction = (0,0,-1)
  Length = 500
  Length2 = 5
  Profile = -> Sketch037
  ReferenceAxis = -> Sketch037 [N_Axis]
  Refine = true
  Suppressed = false
  Type = 0
FEATURE [Sketcher::SketchObject] Sketch038
  ArcFitTolerance = 1e-06
  AttachmentSupport = -> [Pocket009]
  FullyConstrained = false
  MakeInternals = false
  MapMode = 5
  Placement = pos=(0,0,-600) rot=(1,0,0;3.14159rad)
  sketch-geometry (4):
    g0: LineSegment StartX=205.91 StartY=131.665 StartZ=0 EndX=205.91 EndY=-125.888 EndZ=0
    g1: LineSegment StartX=205.91 StartY=-125.888 StartZ=0 EndX=1205.07 EndY=-125.888 EndZ=0
    g2: LineSegment StartX=1205.07 StartY=-125.888 StartZ=0 EndX=1205.07 EndY=131.665 EndZ=0
    g3: LineSegment StartX=1205.07 StartY=131.665 StartZ=0 EndX=205.91 EndY=131.665 EndZ=0
  constraints (8):
    c: Coincident(g0,g1)
    c: Coincident(g1,g2)
    c: Coincident(g2,g3)
    c: Coincident(g3,g0)
    c: Vertical(g0)
    c: Vertical(g2)
    c: Horizontal(g1)
    c: Horizontal(g3)
FEATURE [PartDesign::Pocket] Pocket010
  BaseFeature = -> Pocket009
  Direction = (0,0,1)
  Length = 90
  Length2 = 5
  Profile = -> Sketch038
  ReferenceAxis = -> Sketch038 [N_Axis]
  Refine = true
  Suppressed = false
  Type = 0
FEATURE [PartDesign::Body] Body005
  AllowCompound = false
  Group = -> [Sketch020,Sketch021,AdditiveLoft005,Sketch022,Sketch023,SubtractiveLoft005,Sketch037,Pocket009,Sketch038,Pocket010]
  Origin = -> Origin005
  Tip = -> Pocket010
FEATURE [PartDesign::Plane] DatumPlane
  AttachmentOffset = pos=(0,0,0) rot=(0,-1,0;0.785398rad)
  AttachmentSupport = -> [AdditiveLoft006]
  Length = 82.6027
  MapMode = 5
  Placement = pos=(0,0,0) rot=(0,-1,0;0.785398rad)
  ResizeMode = 0
  Width = 61.8921
FEATURE [Sketcher::SketchObject] Sketch039
  ArcFitTolerance = 1e-06
  AttachmentSupport = -> [DatumPlane]
  FullyConstrained = false
  MakeInternals = false
  MapMode = 5
  Placement = pos=(0,0,0) rot=(0,-1,0;0.785398rad)
  sketch-geometry (1):
    g0: Circle CenterX=37.3314 CenterY=5.35248 CenterZ=0 NormalX=0 NormalY=0 NormalZ=1 AngleXU=0 Radius=4.05
  constraints (1):
    c: Diameter(g0) = 8.1
FEATURE [PartDesign::Pocket] Pocket011
  BaseFeature = -> AdditiveLoft006
  Direction = (0.707107,0,-0.707107)
  Length = 1000
  Length2 = 5
  Profile = -> Sketch039
  ReferenceAxis = -> Sketch039 [N_Axis]
  Refine = true
  Suppressed = false
  Type = 0
FEATURE [PartDesign::Body] Body006
  AllowCompound = false
  Group = -> [Sketch024,Sketch025,AdditiveLoft006,DatumPlane,Sketch039,Pocket011]
  Origin = -> Origin006
  Tip = -> Pocket011
